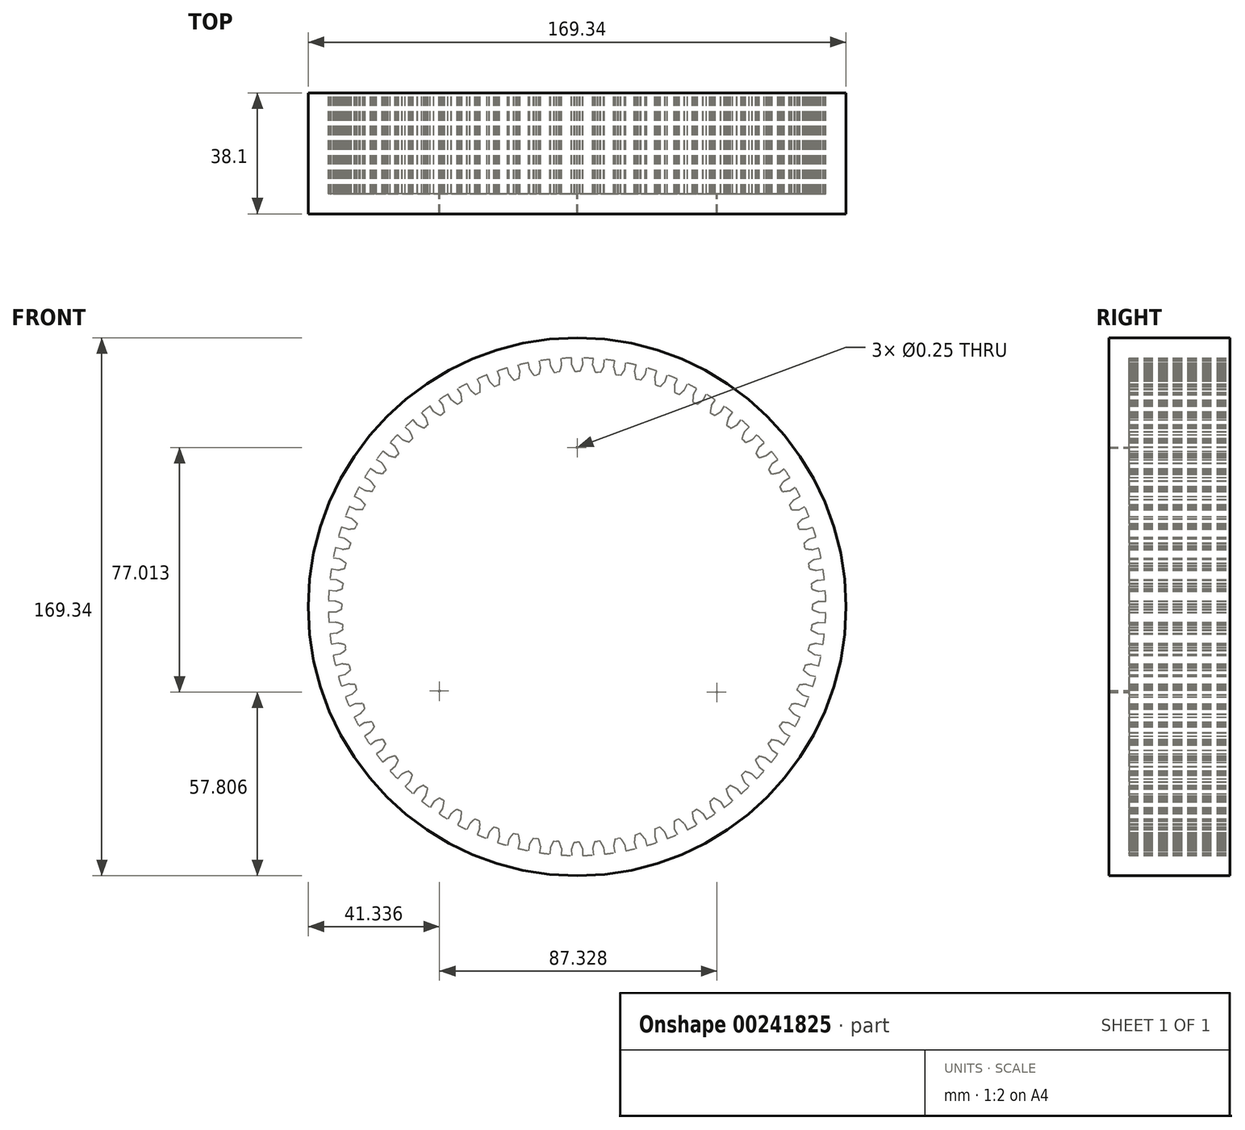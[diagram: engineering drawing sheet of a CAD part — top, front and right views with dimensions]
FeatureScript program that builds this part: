
annotation { "Feature Type Name" : "Feature", "Feature Type Description" : "" }
export const myFeature = defineFeature(function(context is Context, id is Id, definition is map)
    precondition{}
    {
        {
            var Q0;
            Q0=qCreatedBy(makeId("Front.planeOp"),FACE);
            var sketch = newSketch(context, id + "F0", { "sketchPlane" : qUnion([Q0])});
            skCircle(sketch, "E0", {"center": v(0, 0) * mm, "radius": 78.32 * mm});
            skPoint(sketch, "E1", {"position": v(1.7, -156.6) * mm});
            skArc(sketch, "E2.trimOffspring", {"start": v(1.7, -76.18) * mm, "mid": v(1.25, -75.12) * mm, "end": v(0.73, -74.08) * mm});
            skLineSegment(sketch, "E3", {"start": v(1.7, -76.18) * mm, "end": v(1.75, -78.3) * mm});
            skLineSegment(sketch, "E4", {"start": v(0.73, -74.08) * mm, "end": v(-0.1, -74.09) * mm});
            skLineSegment(sketch, "E5.MirrorCS", {"start": v(-0.92, -74.12) * mm, "end": v(-0.1, -74.09) * mm});
            skArc(sketch, "E6.MirrorCS", {"start": v(-1.8, -76.26) * mm, "mid": v(-1.4, -75.17) * mm, "end": v(-0.92, -74.12) * mm});
            skLineSegment(sketch, "E7.MirrorCS", {"start": v(-1.8, -76.26) * mm, "end": v(-1.76, -78.3) * mm});
            skLineSegment(sketch, "E8.1.0", {"start": v(4.85, -76.12) * mm, "end": v(5.08, -78.15) * mm});
            skArc(sketch, "E8.1.1", {"start": v(4.85, -76.12) * mm, "mid": v(5.17, -75) * mm, "end": v(5.55, -73.91) * mm});
            skLineSegment(sketch, "E8.1.2", {"start": v(5.55, -73.91) * mm, "end": v(6.37, -73.81) * mm});
            skLineSegment(sketch, "E8.1.3", {"start": v(7.19, -73.73) * mm, "end": v(6.37, -73.81) * mm});
            skArc(sketch, "E8.1.4", {"start": v(8.34, -75.74) * mm, "mid": v(7.8, -74.72) * mm, "end": v(7.19, -73.73) * mm});
            skLineSegment(sketch, "E8.1.5", {"start": v(8.34, -75.74) * mm, "end": v(8.57, -77.85) * mm});
            skLineSegment(sketch, "E8.2.0", {"start": v(11.47, -75.41) * mm, "end": v(11.87, -77.41) * mm});
            skArc(sketch, "E8.2.1", {"start": v(11.47, -75.41) * mm, "mid": v(11.68, -74.27) * mm, "end": v(11.97, -73.15) * mm});
            skLineSegment(sketch, "E8.2.2", {"start": v(11.97, -73.15) * mm, "end": v(12.77, -72.98) * mm});
            skLineSegment(sketch, "E8.2.3", {"start": v(13.58, -72.83) * mm, "end": v(12.77, -72.98) * mm});
            skArc(sketch, "E8.2.4", {"start": v(14.91, -74.73) * mm, "mid": v(14.28, -73.76) * mm, "end": v(13.58, -72.83) * mm});
            skLineSegment(sketch, "E8.2.5", {"start": v(14.91, -74.73) * mm, "end": v(15.32, -76.8) * mm});
            skLineSegment(sketch, "E8.3.0", {"start": v(18, -74.12) * mm, "end": v(18.57, -76.08) * mm});
            skArc(sketch, "E8.3.1", {"start": v(18, -74.12) * mm, "mid": v(18.11, -72.97) * mm, "end": v(18.3, -71.83) * mm});
            skLineSegment(sketch, "E8.3.2", {"start": v(18.3, -71.83) * mm, "end": v(19.09, -71.59) * mm});
            skLineSegment(sketch, "E8.3.3", {"start": v(19.88, -71.37) * mm, "end": v(19.09, -71.59) * mm});
            skArc(sketch, "E8.3.4", {"start": v(21.37, -73.14) * mm, "mid": v(20.65, -72.23) * mm, "end": v(19.88, -71.37) * mm});
            skLineSegment(sketch, "E8.3.5", {"start": v(21.37, -73.14) * mm, "end": v(21.96, -75.17) * mm});
            skLineSegment(sketch, "E8.4.0", {"start": v(24.4, -72.27) * mm, "end": v(25.13, -74.17) * mm});
            skArc(sketch, "E8.4.1", {"start": v(24.4, -72.27) * mm, "mid": v(24.4, -71.11) * mm, "end": v(24.49, -69.96) * mm});
            skLineSegment(sketch, "E8.4.2", {"start": v(24.49, -69.96) * mm, "end": v(25.25, -69.65) * mm});
            skLineSegment(sketch, "E8.4.3", {"start": v(26.02, -69.36) * mm, "end": v(25.25, -69.65) * mm});
            skArc(sketch, "E8.4.4", {"start": v(27.66, -71) * mm, "mid": v(26.87, -70.16) * mm, "end": v(26.02, -69.36) * mm});
            skLineSegment(sketch, "E8.4.5", {"start": v(27.66, -71) * mm, "end": v(28.43, -72.97) * mm});
            skLineSegment(sketch, "E8.5.0", {"start": v(30.6, -69.87) * mm, "end": v(31.5, -71.7) * mm});
            skArc(sketch, "E8.5.1", {"start": v(30.6, -69.87) * mm, "mid": v(30.5, -68.72) * mm, "end": v(30.5, -67.56) * mm});
            skLineSegment(sketch, "E8.5.2", {"start": v(30.5, -67.56) * mm, "end": v(31.23, -67.19) * mm});
            skLineSegment(sketch, "E8.5.3", {"start": v(31.97, -66.83) * mm, "end": v(31.23, -67.19) * mm});
            skArc(sketch, "E8.5.4", {"start": v(33.74, -68.32) * mm, "mid": v(32.88, -67.55) * mm, "end": v(31.97, -66.83) * mm});
            skLineSegment(sketch, "E8.5.5", {"start": v(33.74, -68.32) * mm, "end": v(34.68, -70.22) * mm});
            skLineSegment(sketch, "E8.6.0", {"start": v(36.57, -66.94) * mm, "end": v(37.63, -68.68) * mm});
            skArc(sketch, "E8.6.1", {"start": v(36.57, -66.94) * mm, "mid": v(36.38, -65.8) * mm, "end": v(36.26, -64.64) * mm});
            skLineSegment(sketch, "E8.6.2", {"start": v(36.26, -64.64) * mm, "end": v(36.96, -64.2) * mm});
            skLineSegment(sketch, "E8.6.3", {"start": v(37.67, -63.79) * mm, "end": v(36.96, -64.2) * mm});
            skArc(sketch, "E8.6.4", {"start": v(39.57, -65.12) * mm, "mid": v(38.64, -64.43) * mm, "end": v(37.67, -63.79) * mm});
            skLineSegment(sketch, "E8.6.5", {"start": v(39.57, -65.12) * mm, "end": v(40.67, -66.93) * mm});
            skLineSegment(sketch, "E8.7.0", {"start": v(42.27, -63.5) * mm, "end": v(43.47, -65.14) * mm});
            skArc(sketch, "E8.7.1", {"start": v(42.27, -63.5) * mm, "mid": v(41.98, -62.38) * mm, "end": v(41.76, -61.24) * mm});
            skLineSegment(sketch, "E8.7.2", {"start": v(41.76, -61.24) * mm, "end": v(42.42, -60.74) * mm});
            skLineSegment(sketch, "E8.7.3", {"start": v(43.09, -60.26) * mm, "end": v(42.42, -60.74) * mm});
            skArc(sketch, "E8.7.4", {"start": v(45.1, -61.42) * mm, "mid": v(44.11, -60.81) * mm, "end": v(43.09, -60.26) * mm});
            skLineSegment(sketch, "E8.7.5", {"start": v(45.1, -61.42) * mm, "end": v(46.35, -63.13) * mm});
            skLineSegment(sketch, "E8.8.0", {"start": v(47.64, -59.57) * mm, "end": v(48.98, -61.1) * mm});
            skArc(sketch, "E8.8.1", {"start": v(47.64, -59.57) * mm, "mid": v(47.25, -58.48) * mm, "end": v(46.94, -57.36) * mm});
            skLineSegment(sketch, "E8.8.2", {"start": v(46.94, -57.36) * mm, "end": v(47.55, -56.81) * mm});
            skLineSegment(sketch, "E8.8.3", {"start": v(48.18, -56.28) * mm, "end": v(47.55, -56.81) * mm});
            skArc(sketch, "E8.8.4", {"start": v(50.28, -57.26) * mm, "mid": v(49.24, -56.74) * mm, "end": v(48.18, -56.28) * mm});
            skLineSegment(sketch, "E8.8.5", {"start": v(50.28, -57.26) * mm, "end": v(51.67, -58.85) * mm});
            skLineSegment(sketch, "E8.9.0", {"start": v(52.65, -55.2) * mm, "end": v(54.12, -56.6) * mm});
            skArc(sketch, "E8.9.1", {"start": v(52.65, -55.2) * mm, "mid": v(52.17, -54.14) * mm, "end": v(51.76, -53.06) * mm});
            skLineSegment(sketch, "E8.9.2", {"start": v(51.76, -53.06) * mm, "end": v(52.32, -52.45) * mm});
            skLineSegment(sketch, "E8.9.3", {"start": v(52.9, -51.86) * mm, "end": v(52.32, -52.45) * mm});
            skArc(sketch, "E8.9.4", {"start": v(55.08, -52.66) * mm, "mid": v(54, -52.23) * mm, "end": v(52.9, -51.86) * mm});
            skLineSegment(sketch, "E8.9.5", {"start": v(55.08, -52.66) * mm, "end": v(56.6, -54.12) * mm});
            skLineSegment(sketch, "E8.10.0", {"start": v(57.26, -50.4) * mm, "end": v(58.85, -51.67) * mm});
            skArc(sketch, "E8.10.1", {"start": v(57.26, -50.4) * mm, "mid": v(56.7, -49.39) * mm, "end": v(56.19, -48.34) * mm});
            skLineSegment(sketch, "E8.10.2", {"start": v(56.19, -48.34) * mm, "end": v(56.7, -47.7) * mm});
            skLineSegment(sketch, "E8.10.3", {"start": v(57.22, -47.06) * mm, "end": v(56.7, -47.7) * mm});
            skArc(sketch, "E8.10.4", {"start": v(59.46, -47.66) * mm, "mid": v(58.35, -47.32) * mm, "end": v(57.22, -47.06) * mm});
            skLineSegment(sketch, "E8.10.5", {"start": v(59.46, -47.66) * mm, "end": v(61.1, -48.98) * mm});
            skLineSegment(sketch, "E8.11.0", {"start": v(61.43, -45.21) * mm, "end": v(63.13, -46.35) * mm});
            skArc(sketch, "E8.11.1", {"start": v(61.43, -45.21) * mm, "mid": v(60.78, -44.26) * mm, "end": v(60.19, -43.26) * mm});
            skLineSegment(sketch, "E8.11.2", {"start": v(60.19, -43.26) * mm, "end": v(60.64, -42.57) * mm});
            skLineSegment(sketch, "E8.11.3", {"start": v(61.1, -41.9) * mm, "end": v(60.64, -42.57) * mm});
            skArc(sketch, "E8.11.4", {"start": v(63.38, -42.3) * mm, "mid": v(62.25, -42.06) * mm, "end": v(61.1, -41.9) * mm});
            skLineSegment(sketch, "E8.11.5", {"start": v(63.38, -42.3) * mm, "end": v(65.14, -43.47) * mm});
            skLineSegment(sketch, "E8.12.0", {"start": v(65.14, -39.69) * mm, "end": v(66.93, -40.67) * mm});
            skArc(sketch, "E8.12.1", {"start": v(65.14, -39.69) * mm, "mid": v(64.4, -38.8) * mm, "end": v(63.73, -37.85) * mm});
            skLineSegment(sketch, "E8.12.2", {"start": v(63.73, -37.85) * mm, "end": v(64.12, -37.12) * mm});
            skLineSegment(sketch, "E8.12.3", {"start": v(64.52, -36.4) * mm, "end": v(64.12, -37.12) * mm});
            skArc(sketch, "E8.12.4", {"start": v(66.83, -36.61) * mm, "mid": v(65.68, -36.47) * mm, "end": v(64.52, -36.4) * mm});
            skLineSegment(sketch, "E8.12.5", {"start": v(66.83, -36.61) * mm, "end": v(68.68, -37.63) * mm});
            skLineSegment(sketch, "E8.13.0", {"start": v(68.35, -33.86) * mm, "end": v(70.22, -34.68) * mm});
            skArc(sketch, "E8.13.1", {"start": v(68.35, -33.86) * mm, "mid": v(67.54, -33.03) * mm, "end": v(66.78, -32.15) * mm});
            skLineSegment(sketch, "E8.13.2", {"start": v(66.78, -32.15) * mm, "end": v(67.1, -31.4) * mm});
            skLineSegment(sketch, "E8.13.3", {"start": v(67.45, -30.64) * mm, "end": v(67.1, -31.4) * mm});
            skArc(sketch, "E8.13.4", {"start": v(69.77, -30.65) * mm, "mid": v(68.6, -30.61) * mm, "end": v(67.45, -30.64) * mm});
            skLineSegment(sketch, "E8.13.5", {"start": v(69.77, -30.65) * mm, "end": v(71.7, -31.5) * mm});
            skLineSegment(sketch, "E8.14.0", {"start": v(71.04, -27.77) * mm, "end": v(72.97, -28.43) * mm});
            skArc(sketch, "E8.14.1", {"start": v(71.04, -27.77) * mm, "mid": v(70.16, -27.02) * mm, "end": v(69.33, -26.2) * mm});
            skLineSegment(sketch, "E8.14.2", {"start": v(69.33, -26.2) * mm, "end": v(69.59, -25.43) * mm});
            skLineSegment(sketch, "E8.14.3", {"start": v(69.86, -24.65) * mm, "end": v(69.59, -25.43) * mm});
            skArc(sketch, "E8.14.4", {"start": v(72.17, -24.45) * mm, "mid": v(71.01, -24.51) * mm, "end": v(69.86, -24.65) * mm});
            skLineSegment(sketch, "E8.14.5", {"start": v(72.17, -24.45) * mm, "end": v(74.17, -25.13) * mm});
            skLineSegment(sketch, "E8.15.0", {"start": v(73.2, -21.48) * mm, "end": v(75.17, -21.96) * mm});
            skArc(sketch, "E8.15.1", {"start": v(73.2, -21.48) * mm, "mid": v(72.25, -20.8) * mm, "end": v(71.35, -20.07) * mm});
            skLineSegment(sketch, "E8.15.2", {"start": v(71.35, -20.07) * mm, "end": v(71.54, -19.26) * mm});
            skLineSegment(sketch, "E8.15.3", {"start": v(71.74, -18.47) * mm, "end": v(71.54, -19.26) * mm});
            skArc(sketch, "E8.15.4", {"start": v(74.03, -18.07) * mm, "mid": v(72.88, -18.23) * mm, "end": v(71.74, -18.47) * mm});
            skLineSegment(sketch, "E8.15.5", {"start": v(74.03, -18.07) * mm, "end": v(76.08, -18.57) * mm});
            skLineSegment(sketch, "E8.16.0", {"start": v(74.79, -15.01) * mm, "end": v(76.8, -15.32) * mm});
            skArc(sketch, "E8.16.1", {"start": v(74.79, -15.01) * mm, "mid": v(73.79, -14.42) * mm, "end": v(72.83, -13.77) * mm});
            skLineSegment(sketch, "E8.16.2", {"start": v(72.83, -13.77) * mm, "end": v(72.95, -12.96) * mm});
            skLineSegment(sketch, "E8.16.3", {"start": v(73.08, -12.14) * mm, "end": v(72.95, -12.96) * mm});
            skArc(sketch, "E8.16.4", {"start": v(75.32, -11.55) * mm, "mid": v(74.2, -11.81) * mm, "end": v(73.08, -12.14) * mm});
            skLineSegment(sketch, "E8.16.5", {"start": v(75.32, -11.55) * mm, "end": v(77.41, -11.87) * mm});
            skLineSegment(sketch, "E8.17.0", {"start": v(75.81, -8.44) * mm, "end": v(77.85, -8.57) * mm});
            skArc(sketch, "E8.17.1", {"start": v(75.81, -8.44) * mm, "mid": v(74.77, -7.94) * mm, "end": v(73.75, -7.37) * mm});
            skLineSegment(sketch, "E8.17.2", {"start": v(73.75, -7.37) * mm, "end": v(73.8, -6.55) * mm});
            skLineSegment(sketch, "E8.17.3", {"start": v(73.86, -5.73) * mm, "end": v(73.8, -6.55) * mm});
            skArc(sketch, "E8.17.4", {"start": v(76.04, -4.94) * mm, "mid": v(74.94, -5.3) * mm, "end": v(73.86, -5.73) * mm});
            skLineSegment(sketch, "E8.17.5", {"start": v(76.04, -4.94) * mm, "end": v(78.15, -5.08) * mm});
            skLineSegment(sketch, "E8.18.0", {"start": v(76.26, -1.8) * mm, "end": v(78.3, -1.76) * mm});
            skArc(sketch, "E8.18.1", {"start": v(76.26, -1.8) * mm, "mid": v(75.17, -1.4) * mm, "end": v(74.12, -0.92) * mm});
            skLineSegment(sketch, "E8.18.2", {"start": v(74.12, -0.92) * mm, "end": v(74.09, -0.1) * mm});
            skLineSegment(sketch, "E8.18.3", {"start": v(74.08, 0.73) * mm, "end": v(74.09, -0.1) * mm});
            skArc(sketch, "E8.18.4", {"start": v(76.18, 1.7) * mm, "mid": v(75.12, 1.25) * mm, "end": v(74.08, 0.73) * mm});
            skLineSegment(sketch, "E8.18.5", {"start": v(76.18, 1.7) * mm, "end": v(78.3, 1.75) * mm});
            skLineSegment(sketch, "E8.19.0", {"start": v(76.12, 4.85) * mm, "end": v(78.15, 5.08) * mm});
            skArc(sketch, "E8.19.1", {"start": v(76.12, 4.85) * mm, "mid": v(75, 5.17) * mm, "end": v(73.91, 5.55) * mm});
            skLineSegment(sketch, "E8.19.2", {"start": v(73.91, 5.55) * mm, "end": v(73.81, 6.37) * mm});
            skLineSegment(sketch, "E8.19.3", {"start": v(73.73, 7.19) * mm, "end": v(73.81, 6.37) * mm});
            skArc(sketch, "E8.19.4", {"start": v(75.74, 8.34) * mm, "mid": v(74.72, 7.8) * mm, "end": v(73.73, 7.19) * mm});
            skLineSegment(sketch, "E8.19.5", {"start": v(75.74, 8.34) * mm, "end": v(77.85, 8.57) * mm});
            skLineSegment(sketch, "E8.20.0", {"start": v(75.41, 11.47) * mm, "end": v(77.41, 11.87) * mm});
            skArc(sketch, "E8.20.1", {"start": v(75.41, 11.47) * mm, "mid": v(74.27, 11.68) * mm, "end": v(73.15, 11.97) * mm});
            skLineSegment(sketch, "E8.20.2", {"start": v(73.15, 11.97) * mm, "end": v(72.98, 12.77) * mm});
            skLineSegment(sketch, "E8.20.3", {"start": v(72.83, 13.58) * mm, "end": v(72.98, 12.77) * mm});
            skArc(sketch, "E8.20.4", {"start": v(74.73, 14.91) * mm, "mid": v(73.76, 14.28) * mm, "end": v(72.83, 13.58) * mm});
            skLineSegment(sketch, "E8.20.5", {"start": v(74.73, 14.91) * mm, "end": v(76.8, 15.32) * mm});
            skLineSegment(sketch, "E8.21.0", {"start": v(74.12, 18) * mm, "end": v(76.08, 18.57) * mm});
            skArc(sketch, "E8.21.1", {"start": v(74.12, 18) * mm, "mid": v(72.97, 18.11) * mm, "end": v(71.83, 18.3) * mm});
            skLineSegment(sketch, "E8.21.2", {"start": v(71.83, 18.3) * mm, "end": v(71.59, 19.09) * mm});
            skLineSegment(sketch, "E8.21.3", {"start": v(71.37, 19.88) * mm, "end": v(71.59, 19.09) * mm});
            skArc(sketch, "E8.21.4", {"start": v(73.14, 21.37) * mm, "mid": v(72.23, 20.65) * mm, "end": v(71.37, 19.88) * mm});
            skLineSegment(sketch, "E8.21.5", {"start": v(73.14, 21.37) * mm, "end": v(75.17, 21.96) * mm});
            skLineSegment(sketch, "E8.22.0", {"start": v(72.27, 24.4) * mm, "end": v(74.17, 25.13) * mm});
            skArc(sketch, "E8.22.1", {"start": v(72.27, 24.4) * mm, "mid": v(71.11, 24.4) * mm, "end": v(69.96, 24.49) * mm});
            skLineSegment(sketch, "E8.22.2", {"start": v(69.96, 24.49) * mm, "end": v(69.65, 25.25) * mm});
            skLineSegment(sketch, "E8.22.3", {"start": v(69.36, 26.02) * mm, "end": v(69.65, 25.25) * mm});
            skArc(sketch, "E8.22.4", {"start": v(71, 27.66) * mm, "mid": v(70.16, 26.87) * mm, "end": v(69.36, 26.02) * mm});
            skLineSegment(sketch, "E8.22.5", {"start": v(71, 27.66) * mm, "end": v(72.97, 28.43) * mm});
            skLineSegment(sketch, "E8.23.0", {"start": v(69.87, 30.6) * mm, "end": v(71.7, 31.5) * mm});
            skArc(sketch, "E8.23.1", {"start": v(69.87, 30.6) * mm, "mid": v(68.72, 30.5) * mm, "end": v(67.56, 30.5) * mm});
            skLineSegment(sketch, "E8.23.2", {"start": v(67.56, 30.5) * mm, "end": v(67.19, 31.23) * mm});
            skLineSegment(sketch, "E8.23.3", {"start": v(66.83, 31.97) * mm, "end": v(67.19, 31.23) * mm});
            skArc(sketch, "E8.23.4", {"start": v(68.32, 33.74) * mm, "mid": v(67.55, 32.88) * mm, "end": v(66.83, 31.97) * mm});
            skLineSegment(sketch, "E8.23.5", {"start": v(68.32, 33.74) * mm, "end": v(70.22, 34.68) * mm});
            skLineSegment(sketch, "E8.24.0", {"start": v(66.94, 36.57) * mm, "end": v(68.68, 37.63) * mm});
            skArc(sketch, "E8.24.1", {"start": v(66.94, 36.57) * mm, "mid": v(65.8, 36.38) * mm, "end": v(64.64, 36.26) * mm});
            skLineSegment(sketch, "E8.24.2", {"start": v(64.64, 36.26) * mm, "end": v(64.2, 36.96) * mm});
            skLineSegment(sketch, "E8.24.3", {"start": v(63.79, 37.67) * mm, "end": v(64.2, 36.96) * mm});
            skArc(sketch, "E8.24.4", {"start": v(65.12, 39.57) * mm, "mid": v(64.43, 38.64) * mm, "end": v(63.79, 37.67) * mm});
            skLineSegment(sketch, "E8.24.5", {"start": v(65.12, 39.57) * mm, "end": v(66.93, 40.67) * mm});
            skLineSegment(sketch, "E8.25.0", {"start": v(63.5, 42.27) * mm, "end": v(65.14, 43.47) * mm});
            skArc(sketch, "E8.25.1", {"start": v(63.5, 42.27) * mm, "mid": v(62.38, 41.98) * mm, "end": v(61.24, 41.76) * mm});
            skLineSegment(sketch, "E8.25.2", {"start": v(61.24, 41.76) * mm, "end": v(60.74, 42.42) * mm});
            skLineSegment(sketch, "E8.25.3", {"start": v(60.26, 43.09) * mm, "end": v(60.74, 42.42) * mm});
            skArc(sketch, "E8.25.4", {"start": v(61.42, 45.1) * mm, "mid": v(60.81, 44.11) * mm, "end": v(60.26, 43.09) * mm});
            skLineSegment(sketch, "E8.25.5", {"start": v(61.42, 45.1) * mm, "end": v(63.13, 46.35) * mm});
            skLineSegment(sketch, "E8.26.0", {"start": v(59.57, 47.64) * mm, "end": v(61.1, 48.98) * mm});
            skArc(sketch, "E8.26.1", {"start": v(59.57, 47.64) * mm, "mid": v(58.48, 47.25) * mm, "end": v(57.36, 46.94) * mm});
            skLineSegment(sketch, "E8.26.2", {"start": v(57.36, 46.94) * mm, "end": v(56.81, 47.55) * mm});
            skLineSegment(sketch, "E8.26.3", {"start": v(56.28, 48.18) * mm, "end": v(56.81, 47.55) * mm});
            skArc(sketch, "E8.26.4", {"start": v(57.26, 50.28) * mm, "mid": v(56.74, 49.24) * mm, "end": v(56.28, 48.18) * mm});
            skLineSegment(sketch, "E8.26.5", {"start": v(57.26, 50.28) * mm, "end": v(58.85, 51.67) * mm});
            skLineSegment(sketch, "E8.27.0", {"start": v(55.2, 52.65) * mm, "end": v(56.6, 54.12) * mm});
            skArc(sketch, "E8.27.1", {"start": v(55.2, 52.65) * mm, "mid": v(54.14, 52.17) * mm, "end": v(53.06, 51.76) * mm});
            skLineSegment(sketch, "E8.27.2", {"start": v(53.06, 51.76) * mm, "end": v(52.45, 52.32) * mm});
            skLineSegment(sketch, "E8.27.3", {"start": v(51.86, 52.9) * mm, "end": v(52.45, 52.32) * mm});
            skArc(sketch, "E8.27.4", {"start": v(52.66, 55.08) * mm, "mid": v(52.23, 54) * mm, "end": v(51.86, 52.9) * mm});
            skLineSegment(sketch, "E8.27.5", {"start": v(52.66, 55.08) * mm, "end": v(54.12, 56.6) * mm});
            skLineSegment(sketch, "E8.28.0", {"start": v(50.4, 57.26) * mm, "end": v(51.67, 58.85) * mm});
            skArc(sketch, "E8.28.1", {"start": v(50.4, 57.26) * mm, "mid": v(49.39, 56.7) * mm, "end": v(48.34, 56.19) * mm});
            skLineSegment(sketch, "E8.28.2", {"start": v(48.34, 56.19) * mm, "end": v(47.7, 56.7) * mm});
            skLineSegment(sketch, "E8.28.3", {"start": v(47.06, 57.22) * mm, "end": v(47.7, 56.7) * mm});
            skArc(sketch, "E8.28.4", {"start": v(47.66, 59.46) * mm, "mid": v(47.32, 58.35) * mm, "end": v(47.06, 57.22) * mm});
            skLineSegment(sketch, "E8.28.5", {"start": v(47.66, 59.46) * mm, "end": v(48.98, 61.1) * mm});
            skLineSegment(sketch, "E8.29.0", {"start": v(45.21, 61.43) * mm, "end": v(46.35, 63.13) * mm});
            skArc(sketch, "E8.29.1", {"start": v(45.21, 61.43) * mm, "mid": v(44.26, 60.78) * mm, "end": v(43.26, 60.19) * mm});
            skLineSegment(sketch, "E8.29.2", {"start": v(43.26, 60.19) * mm, "end": v(42.57, 60.64) * mm});
            skLineSegment(sketch, "E8.29.3", {"start": v(41.9, 61.1) * mm, "end": v(42.57, 60.64) * mm});
            skArc(sketch, "E8.29.4", {"start": v(42.3, 63.38) * mm, "mid": v(42.06, 62.25) * mm, "end": v(41.9, 61.1) * mm});
            skLineSegment(sketch, "E8.29.5", {"start": v(42.3, 63.38) * mm, "end": v(43.47, 65.14) * mm});
            skLineSegment(sketch, "E8.30.0", {"start": v(39.69, 65.14) * mm, "end": v(40.67, 66.93) * mm});
            skArc(sketch, "E8.30.1", {"start": v(39.69, 65.14) * mm, "mid": v(38.8, 64.4) * mm, "end": v(37.85, 63.73) * mm});
            skLineSegment(sketch, "E8.30.2", {"start": v(37.85, 63.73) * mm, "end": v(37.12, 64.12) * mm});
            skLineSegment(sketch, "E8.30.3", {"start": v(36.4, 64.52) * mm, "end": v(37.12, 64.12) * mm});
            skArc(sketch, "E8.30.4", {"start": v(36.61, 66.83) * mm, "mid": v(36.47, 65.68) * mm, "end": v(36.4, 64.52) * mm});
            skLineSegment(sketch, "E8.30.5", {"start": v(36.61, 66.83) * mm, "end": v(37.63, 68.68) * mm});
            skLineSegment(sketch, "E8.31.0", {"start": v(33.86, 68.35) * mm, "end": v(34.68, 70.22) * mm});
            skArc(sketch, "E8.31.1", {"start": v(33.86, 68.35) * mm, "mid": v(33.03, 67.54) * mm, "end": v(32.15, 66.78) * mm});
            skLineSegment(sketch, "E8.31.2", {"start": v(32.15, 66.78) * mm, "end": v(31.4, 67.1) * mm});
            skLineSegment(sketch, "E8.31.3", {"start": v(30.64, 67.45) * mm, "end": v(31.4, 67.1) * mm});
            skArc(sketch, "E8.31.4", {"start": v(30.65, 69.77) * mm, "mid": v(30.61, 68.6) * mm, "end": v(30.64, 67.45) * mm});
            skLineSegment(sketch, "E8.31.5", {"start": v(30.65, 69.77) * mm, "end": v(31.5, 71.7) * mm});
            skLineSegment(sketch, "E8.32.0", {"start": v(27.77, 71.04) * mm, "end": v(28.43, 72.97) * mm});
            skArc(sketch, "E8.32.1", {"start": v(27.77, 71.04) * mm, "mid": v(27.02, 70.16) * mm, "end": v(26.2, 69.33) * mm});
            skLineSegment(sketch, "E8.32.2", {"start": v(26.2, 69.33) * mm, "end": v(25.43, 69.59) * mm});
            skLineSegment(sketch, "E8.32.3", {"start": v(24.65, 69.86) * mm, "end": v(25.43, 69.59) * mm});
            skArc(sketch, "E8.32.4", {"start": v(24.45, 72.17) * mm, "mid": v(24.51, 71.01) * mm, "end": v(24.65, 69.86) * mm});
            skLineSegment(sketch, "E8.32.5", {"start": v(24.45, 72.17) * mm, "end": v(25.13, 74.17) * mm});
            skLineSegment(sketch, "E8.33.0", {"start": v(21.48, 73.2) * mm, "end": v(21.96, 75.17) * mm});
            skArc(sketch, "E8.33.1", {"start": v(21.48, 73.2) * mm, "mid": v(20.8, 72.25) * mm, "end": v(20.07, 71.35) * mm});
            skLineSegment(sketch, "E8.33.2", {"start": v(20.07, 71.35) * mm, "end": v(19.26, 71.54) * mm});
            skLineSegment(sketch, "E8.33.3", {"start": v(18.47, 71.74) * mm, "end": v(19.26, 71.54) * mm});
            skArc(sketch, "E8.33.4", {"start": v(18.07, 74.03) * mm, "mid": v(18.23, 72.88) * mm, "end": v(18.47, 71.74) * mm});
            skLineSegment(sketch, "E8.33.5", {"start": v(18.07, 74.03) * mm, "end": v(18.57, 76.08) * mm});
            skLineSegment(sketch, "E8.34.0", {"start": v(15.01, 74.79) * mm, "end": v(15.32, 76.8) * mm});
            skArc(sketch, "E8.34.1", {"start": v(15.01, 74.79) * mm, "mid": v(14.42, 73.79) * mm, "end": v(13.77, 72.83) * mm});
            skLineSegment(sketch, "E8.34.2", {"start": v(13.77, 72.83) * mm, "end": v(12.96, 72.95) * mm});
            skLineSegment(sketch, "E8.34.3", {"start": v(12.14, 73.08) * mm, "end": v(12.96, 72.95) * mm});
            skArc(sketch, "E8.34.4", {"start": v(11.55, 75.32) * mm, "mid": v(11.81, 74.2) * mm, "end": v(12.14, 73.08) * mm});
            skLineSegment(sketch, "E8.34.5", {"start": v(11.55, 75.32) * mm, "end": v(11.87, 77.41) * mm});
            skLineSegment(sketch, "E8.35.0", {"start": v(8.44, 75.81) * mm, "end": v(8.57, 77.85) * mm});
            skArc(sketch, "E8.35.1", {"start": v(8.44, 75.81) * mm, "mid": v(7.94, 74.77) * mm, "end": v(7.37, 73.75) * mm});
            skLineSegment(sketch, "E8.35.2", {"start": v(7.37, 73.75) * mm, "end": v(6.55, 73.8) * mm});
            skLineSegment(sketch, "E8.35.3", {"start": v(5.73, 73.86) * mm, "end": v(6.55, 73.8) * mm});
            skArc(sketch, "E8.35.4", {"start": v(4.94, 76.04) * mm, "mid": v(5.3, 74.94) * mm, "end": v(5.73, 73.86) * mm});
            skLineSegment(sketch, "E8.35.5", {"start": v(4.94, 76.04) * mm, "end": v(5.08, 78.15) * mm});
            skLineSegment(sketch, "E8.36.0", {"start": v(1.8, 76.26) * mm, "end": v(1.76, 78.3) * mm});
            skArc(sketch, "E8.36.1", {"start": v(1.8, 76.26) * mm, "mid": v(1.4, 75.17) * mm, "end": v(0.92, 74.12) * mm});
            skLineSegment(sketch, "E8.36.2", {"start": v(0.92, 74.12) * mm, "end": v(0.1, 74.09) * mm});
            skLineSegment(sketch, "E8.36.3", {"start": v(-0.73, 74.08) * mm, "end": v(0.1, 74.09) * mm});
            skArc(sketch, "E8.36.4", {"start": v(-1.7, 76.18) * mm, "mid": v(-1.25, 75.12) * mm, "end": v(-0.73, 74.08) * mm});
            skLineSegment(sketch, "E8.36.5", {"start": v(-1.7, 76.18) * mm, "end": v(-1.75, 78.3) * mm});
            skLineSegment(sketch, "E8.37.0", {"start": v(-4.85, 76.12) * mm, "end": v(-5.08, 78.15) * mm});
            skArc(sketch, "E8.37.1", {"start": v(-4.85, 76.12) * mm, "mid": v(-5.17, 75) * mm, "end": v(-5.55, 73.91) * mm});
            skLineSegment(sketch, "E8.37.2", {"start": v(-5.55, 73.91) * mm, "end": v(-6.37, 73.81) * mm});
            skLineSegment(sketch, "E8.37.3", {"start": v(-7.19, 73.73) * mm, "end": v(-6.37, 73.81) * mm});
            skArc(sketch, "E8.37.4", {"start": v(-8.34, 75.74) * mm, "mid": v(-7.8, 74.72) * mm, "end": v(-7.19, 73.73) * mm});
            skLineSegment(sketch, "E8.37.5", {"start": v(-8.34, 75.74) * mm, "end": v(-8.57, 77.85) * mm});
            skLineSegment(sketch, "E8.38.0", {"start": v(-11.47, 75.41) * mm, "end": v(-11.87, 77.41) * mm});
            skArc(sketch, "E8.38.1", {"start": v(-11.47, 75.41) * mm, "mid": v(-11.68, 74.27) * mm, "end": v(-11.97, 73.15) * mm});
            skLineSegment(sketch, "E8.38.2", {"start": v(-11.97, 73.15) * mm, "end": v(-12.77, 72.98) * mm});
            skLineSegment(sketch, "E8.38.3", {"start": v(-13.58, 72.83) * mm, "end": v(-12.77, 72.98) * mm});
            skArc(sketch, "E8.38.4", {"start": v(-14.91, 74.73) * mm, "mid": v(-14.28, 73.76) * mm, "end": v(-13.58, 72.83) * mm});
            skLineSegment(sketch, "E8.38.5", {"start": v(-14.91, 74.73) * mm, "end": v(-15.32, 76.8) * mm});
            skLineSegment(sketch, "E8.39.0", {"start": v(-18, 74.12) * mm, "end": v(-18.57, 76.08) * mm});
            skArc(sketch, "E8.39.1", {"start": v(-18, 74.12) * mm, "mid": v(-18.11, 72.97) * mm, "end": v(-18.3, 71.83) * mm});
            skLineSegment(sketch, "E8.39.2", {"start": v(-18.3, 71.83) * mm, "end": v(-19.09, 71.59) * mm});
            skLineSegment(sketch, "E8.39.3", {"start": v(-19.88, 71.37) * mm, "end": v(-19.09, 71.59) * mm});
            skArc(sketch, "E8.39.4", {"start": v(-21.37, 73.14) * mm, "mid": v(-20.65, 72.23) * mm, "end": v(-19.88, 71.37) * mm});
            skLineSegment(sketch, "E8.39.5", {"start": v(-21.37, 73.14) * mm, "end": v(-21.96, 75.17) * mm});
            skLineSegment(sketch, "E8.40.0", {"start": v(-24.4, 72.27) * mm, "end": v(-25.13, 74.17) * mm});
            skArc(sketch, "E8.40.1", {"start": v(-24.4, 72.27) * mm, "mid": v(-24.4, 71.11) * mm, "end": v(-24.49, 69.96) * mm});
            skLineSegment(sketch, "E8.40.2", {"start": v(-24.49, 69.96) * mm, "end": v(-25.25, 69.65) * mm});
            skLineSegment(sketch, "E8.40.3", {"start": v(-26.02, 69.36) * mm, "end": v(-25.25, 69.65) * mm});
            skArc(sketch, "E8.40.4", {"start": v(-27.66, 71) * mm, "mid": v(-26.87, 70.16) * mm, "end": v(-26.02, 69.36) * mm});
            skLineSegment(sketch, "E8.40.5", {"start": v(-27.66, 71) * mm, "end": v(-28.43, 72.97) * mm});
            skLineSegment(sketch, "E8.41.0", {"start": v(-30.6, 69.87) * mm, "end": v(-31.5, 71.7) * mm});
            skArc(sketch, "E8.41.1", {"start": v(-30.6, 69.87) * mm, "mid": v(-30.5, 68.72) * mm, "end": v(-30.5, 67.56) * mm});
            skLineSegment(sketch, "E8.41.2", {"start": v(-30.5, 67.56) * mm, "end": v(-31.23, 67.19) * mm});
            skLineSegment(sketch, "E8.41.3", {"start": v(-31.97, 66.83) * mm, "end": v(-31.23, 67.19) * mm});
            skArc(sketch, "E8.41.4", {"start": v(-33.74, 68.32) * mm, "mid": v(-32.88, 67.55) * mm, "end": v(-31.97, 66.83) * mm});
            skLineSegment(sketch, "E8.41.5", {"start": v(-33.74, 68.32) * mm, "end": v(-34.68, 70.22) * mm});
            skLineSegment(sketch, "E8.42.0", {"start": v(-36.57, 66.94) * mm, "end": v(-37.63, 68.68) * mm});
            skArc(sketch, "E8.42.1", {"start": v(-36.57, 66.94) * mm, "mid": v(-36.38, 65.8) * mm, "end": v(-36.26, 64.64) * mm});
            skLineSegment(sketch, "E8.42.2", {"start": v(-36.26, 64.64) * mm, "end": v(-36.96, 64.2) * mm});
            skLineSegment(sketch, "E8.42.3", {"start": v(-37.67, 63.79) * mm, "end": v(-36.96, 64.2) * mm});
            skArc(sketch, "E8.42.4", {"start": v(-39.57, 65.12) * mm, "mid": v(-38.64, 64.43) * mm, "end": v(-37.67, 63.79) * mm});
            skLineSegment(sketch, "E8.42.5", {"start": v(-39.57, 65.12) * mm, "end": v(-40.67, 66.93) * mm});
            skLineSegment(sketch, "E8.43.0", {"start": v(-42.27, 63.5) * mm, "end": v(-43.47, 65.14) * mm});
            skArc(sketch, "E8.43.1", {"start": v(-42.27, 63.5) * mm, "mid": v(-41.98, 62.38) * mm, "end": v(-41.76, 61.24) * mm});
            skLineSegment(sketch, "E8.43.2", {"start": v(-41.76, 61.24) * mm, "end": v(-42.42, 60.74) * mm});
            skLineSegment(sketch, "E8.43.3", {"start": v(-43.09, 60.26) * mm, "end": v(-42.42, 60.74) * mm});
            skArc(sketch, "E8.43.4", {"start": v(-45.1, 61.42) * mm, "mid": v(-44.11, 60.81) * mm, "end": v(-43.09, 60.26) * mm});
            skLineSegment(sketch, "E8.43.5", {"start": v(-45.1, 61.42) * mm, "end": v(-46.35, 63.13) * mm});
            skLineSegment(sketch, "E8.44.0", {"start": v(-47.64, 59.57) * mm, "end": v(-48.98, 61.1) * mm});
            skArc(sketch, "E8.44.1", {"start": v(-47.64, 59.57) * mm, "mid": v(-47.25, 58.48) * mm, "end": v(-46.94, 57.36) * mm});
            skLineSegment(sketch, "E8.44.2", {"start": v(-46.94, 57.36) * mm, "end": v(-47.55, 56.81) * mm});
            skLineSegment(sketch, "E8.44.3", {"start": v(-48.18, 56.28) * mm, "end": v(-47.55, 56.81) * mm});
            skArc(sketch, "E8.44.4", {"start": v(-50.28, 57.26) * mm, "mid": v(-49.24, 56.74) * mm, "end": v(-48.18, 56.28) * mm});
            skLineSegment(sketch, "E8.44.5", {"start": v(-50.28, 57.26) * mm, "end": v(-51.67, 58.85) * mm});
            skLineSegment(sketch, "E8.45.0", {"start": v(-52.65, 55.2) * mm, "end": v(-54.12, 56.6) * mm});
            skArc(sketch, "E8.45.1", {"start": v(-52.65, 55.2) * mm, "mid": v(-52.17, 54.14) * mm, "end": v(-51.76, 53.06) * mm});
            skLineSegment(sketch, "E8.45.2", {"start": v(-51.76, 53.06) * mm, "end": v(-52.32, 52.45) * mm});
            skLineSegment(sketch, "E8.45.3", {"start": v(-52.9, 51.86) * mm, "end": v(-52.32, 52.45) * mm});
            skArc(sketch, "E8.45.4", {"start": v(-55.08, 52.66) * mm, "mid": v(-54, 52.23) * mm, "end": v(-52.9, 51.86) * mm});
            skLineSegment(sketch, "E8.45.5", {"start": v(-55.08, 52.66) * mm, "end": v(-56.6, 54.12) * mm});
            skLineSegment(sketch, "E8.46.0", {"start": v(-57.26, 50.4) * mm, "end": v(-58.85, 51.67) * mm});
            skArc(sketch, "E8.46.1", {"start": v(-57.26, 50.4) * mm, "mid": v(-56.7, 49.39) * mm, "end": v(-56.19, 48.34) * mm});
            skLineSegment(sketch, "E8.46.2", {"start": v(-56.19, 48.34) * mm, "end": v(-56.7, 47.7) * mm});
            skLineSegment(sketch, "E8.46.3", {"start": v(-57.22, 47.06) * mm, "end": v(-56.7, 47.7) * mm});
            skArc(sketch, "E8.46.4", {"start": v(-59.46, 47.66) * mm, "mid": v(-58.35, 47.32) * mm, "end": v(-57.22, 47.06) * mm});
            skLineSegment(sketch, "E8.46.5", {"start": v(-59.46, 47.66) * mm, "end": v(-61.1, 48.98) * mm});
            skLineSegment(sketch, "E8.47.0", {"start": v(-61.43, 45.21) * mm, "end": v(-63.13, 46.35) * mm});
            skArc(sketch, "E8.47.1", {"start": v(-61.43, 45.21) * mm, "mid": v(-60.78, 44.26) * mm, "end": v(-60.19, 43.26) * mm});
            skLineSegment(sketch, "E8.47.2", {"start": v(-60.19, 43.26) * mm, "end": v(-60.64, 42.57) * mm});
            skLineSegment(sketch, "E8.47.3", {"start": v(-61.1, 41.9) * mm, "end": v(-60.64, 42.57) * mm});
            skArc(sketch, "E8.47.4", {"start": v(-63.38, 42.3) * mm, "mid": v(-62.25, 42.06) * mm, "end": v(-61.1, 41.9) * mm});
            skLineSegment(sketch, "E8.47.5", {"start": v(-63.38, 42.3) * mm, "end": v(-65.14, 43.47) * mm});
            skLineSegment(sketch, "E8.48.0", {"start": v(-65.14, 39.69) * mm, "end": v(-66.93, 40.67) * mm});
            skArc(sketch, "E8.48.1", {"start": v(-65.14, 39.69) * mm, "mid": v(-64.4, 38.8) * mm, "end": v(-63.73, 37.85) * mm});
            skLineSegment(sketch, "E8.48.2", {"start": v(-63.73, 37.85) * mm, "end": v(-64.12, 37.12) * mm});
            skLineSegment(sketch, "E8.48.3", {"start": v(-64.52, 36.4) * mm, "end": v(-64.12, 37.12) * mm});
            skArc(sketch, "E8.48.4", {"start": v(-66.83, 36.61) * mm, "mid": v(-65.68, 36.47) * mm, "end": v(-64.52, 36.4) * mm});
            skLineSegment(sketch, "E8.48.5", {"start": v(-66.83, 36.61) * mm, "end": v(-68.68, 37.63) * mm});
            skLineSegment(sketch, "E8.49.0", {"start": v(-68.35, 33.86) * mm, "end": v(-70.22, 34.68) * mm});
            skArc(sketch, "E8.49.1", {"start": v(-68.35, 33.86) * mm, "mid": v(-67.54, 33.03) * mm, "end": v(-66.78, 32.15) * mm});
            skLineSegment(sketch, "E8.49.2", {"start": v(-66.78, 32.15) * mm, "end": v(-67.1, 31.4) * mm});
            skLineSegment(sketch, "E8.49.3", {"start": v(-67.45, 30.64) * mm, "end": v(-67.1, 31.4) * mm});
            skArc(sketch, "E8.49.4", {"start": v(-69.77, 30.65) * mm, "mid": v(-68.6, 30.61) * mm, "end": v(-67.45, 30.64) * mm});
            skLineSegment(sketch, "E8.49.5", {"start": v(-69.77, 30.65) * mm, "end": v(-71.7, 31.5) * mm});
            skLineSegment(sketch, "E8.50.0", {"start": v(-71.04, 27.77) * mm, "end": v(-72.97, 28.43) * mm});
            skArc(sketch, "E8.50.1", {"start": v(-71.04, 27.77) * mm, "mid": v(-70.16, 27.02) * mm, "end": v(-69.33, 26.2) * mm});
            skLineSegment(sketch, "E8.50.2", {"start": v(-69.33, 26.2) * mm, "end": v(-69.59, 25.43) * mm});
            skLineSegment(sketch, "E8.50.3", {"start": v(-69.86, 24.65) * mm, "end": v(-69.59, 25.43) * mm});
            skArc(sketch, "E8.50.4", {"start": v(-72.17, 24.45) * mm, "mid": v(-71.01, 24.51) * mm, "end": v(-69.86, 24.65) * mm});
            skLineSegment(sketch, "E8.50.5", {"start": v(-72.17, 24.45) * mm, "end": v(-74.17, 25.13) * mm});
            skLineSegment(sketch, "E8.51.0", {"start": v(-73.2, 21.48) * mm, "end": v(-75.17, 21.96) * mm});
            skArc(sketch, "E8.51.1", {"start": v(-73.2, 21.48) * mm, "mid": v(-72.25, 20.8) * mm, "end": v(-71.35, 20.07) * mm});
            skLineSegment(sketch, "E8.51.2", {"start": v(-71.35, 20.07) * mm, "end": v(-71.54, 19.26) * mm});
            skLineSegment(sketch, "E8.51.3", {"start": v(-71.74, 18.47) * mm, "end": v(-71.54, 19.26) * mm});
            skArc(sketch, "E8.51.4", {"start": v(-74.03, 18.07) * mm, "mid": v(-72.88, 18.23) * mm, "end": v(-71.74, 18.47) * mm});
            skLineSegment(sketch, "E8.51.5", {"start": v(-74.03, 18.07) * mm, "end": v(-76.08, 18.57) * mm});
            skLineSegment(sketch, "E8.52.0", {"start": v(-74.79, 15.01) * mm, "end": v(-76.8, 15.32) * mm});
            skArc(sketch, "E8.52.1", {"start": v(-74.79, 15.01) * mm, "mid": v(-73.79, 14.42) * mm, "end": v(-72.83, 13.77) * mm});
            skLineSegment(sketch, "E8.52.2", {"start": v(-72.83, 13.77) * mm, "end": v(-72.95, 12.96) * mm});
            skLineSegment(sketch, "E8.52.3", {"start": v(-73.08, 12.14) * mm, "end": v(-72.95, 12.96) * mm});
            skArc(sketch, "E8.52.4", {"start": v(-75.32, 11.55) * mm, "mid": v(-74.2, 11.81) * mm, "end": v(-73.08, 12.14) * mm});
            skLineSegment(sketch, "E8.52.5", {"start": v(-75.32, 11.55) * mm, "end": v(-77.41, 11.87) * mm});
            skLineSegment(sketch, "E8.53.0", {"start": v(-75.81, 8.44) * mm, "end": v(-77.85, 8.57) * mm});
            skArc(sketch, "E8.53.1", {"start": v(-75.81, 8.44) * mm, "mid": v(-74.77, 7.94) * mm, "end": v(-73.75, 7.37) * mm});
            skLineSegment(sketch, "E8.53.2", {"start": v(-73.75, 7.37) * mm, "end": v(-73.8, 6.55) * mm});
            skLineSegment(sketch, "E8.53.3", {"start": v(-73.86, 5.73) * mm, "end": v(-73.8, 6.55) * mm});
            skArc(sketch, "E8.53.4", {"start": v(-76.04, 4.94) * mm, "mid": v(-74.94, 5.3) * mm, "end": v(-73.86, 5.73) * mm});
            skLineSegment(sketch, "E8.53.5", {"start": v(-76.04, 4.94) * mm, "end": v(-78.15, 5.08) * mm});
            skLineSegment(sketch, "E8.54.0", {"start": v(-76.26, 1.8) * mm, "end": v(-78.3, 1.76) * mm});
            skArc(sketch, "E8.54.1", {"start": v(-76.26, 1.8) * mm, "mid": v(-75.17, 1.4) * mm, "end": v(-74.12, 0.92) * mm});
            skLineSegment(sketch, "E8.54.2", {"start": v(-74.12, 0.92) * mm, "end": v(-74.09, 0.1) * mm});
            skLineSegment(sketch, "E8.54.3", {"start": v(-74.08, -0.73) * mm, "end": v(-74.09, 0.1) * mm});
            skArc(sketch, "E8.54.4", {"start": v(-76.18, -1.7) * mm, "mid": v(-75.12, -1.25) * mm, "end": v(-74.08, -0.73) * mm});
            skLineSegment(sketch, "E8.54.5", {"start": v(-76.18, -1.7) * mm, "end": v(-78.3, -1.75) * mm});
            skLineSegment(sketch, "E8.55.0", {"start": v(-76.12, -4.85) * mm, "end": v(-78.15, -5.08) * mm});
            skArc(sketch, "E8.55.1", {"start": v(-76.12, -4.85) * mm, "mid": v(-75, -5.17) * mm, "end": v(-73.91, -5.55) * mm});
            skLineSegment(sketch, "E8.55.2", {"start": v(-73.91, -5.55) * mm, "end": v(-73.81, -6.37) * mm});
            skLineSegment(sketch, "E8.55.3", {"start": v(-73.73, -7.19) * mm, "end": v(-73.81, -6.37) * mm});
            skArc(sketch, "E8.55.4", {"start": v(-75.74, -8.34) * mm, "mid": v(-74.72, -7.8) * mm, "end": v(-73.73, -7.19) * mm});
            skLineSegment(sketch, "E8.55.5", {"start": v(-75.74, -8.34) * mm, "end": v(-77.85, -8.57) * mm});
            skLineSegment(sketch, "E8.56.0", {"start": v(-75.41, -11.47) * mm, "end": v(-77.41, -11.87) * mm});
            skArc(sketch, "E8.56.1", {"start": v(-75.41, -11.47) * mm, "mid": v(-74.27, -11.68) * mm, "end": v(-73.15, -11.97) * mm});
            skLineSegment(sketch, "E8.56.2", {"start": v(-73.15, -11.97) * mm, "end": v(-72.98, -12.77) * mm});
            skLineSegment(sketch, "E8.56.3", {"start": v(-72.83, -13.58) * mm, "end": v(-72.98, -12.77) * mm});
            skArc(sketch, "E8.56.4", {"start": v(-74.73, -14.91) * mm, "mid": v(-73.76, -14.28) * mm, "end": v(-72.83, -13.58) * mm});
            skLineSegment(sketch, "E8.56.5", {"start": v(-74.73, -14.91) * mm, "end": v(-76.8, -15.32) * mm});
            skLineSegment(sketch, "E8.57.0", {"start": v(-74.12, -18) * mm, "end": v(-76.08, -18.57) * mm});
            skArc(sketch, "E8.57.1", {"start": v(-74.12, -18) * mm, "mid": v(-72.97, -18.11) * mm, "end": v(-71.83, -18.3) * mm});
            skLineSegment(sketch, "E8.57.2", {"start": v(-71.83, -18.3) * mm, "end": v(-71.59, -19.09) * mm});
            skLineSegment(sketch, "E8.57.3", {"start": v(-71.37, -19.88) * mm, "end": v(-71.59, -19.09) * mm});
            skArc(sketch, "E8.57.4", {"start": v(-73.14, -21.37) * mm, "mid": v(-72.23, -20.65) * mm, "end": v(-71.37, -19.88) * mm});
            skLineSegment(sketch, "E8.57.5", {"start": v(-73.14, -21.37) * mm, "end": v(-75.17, -21.96) * mm});
            skLineSegment(sketch, "E8.58.0", {"start": v(-72.27, -24.4) * mm, "end": v(-74.17, -25.13) * mm});
            skArc(sketch, "E8.58.1", {"start": v(-72.27, -24.4) * mm, "mid": v(-71.11, -24.4) * mm, "end": v(-69.96, -24.49) * mm});
            skLineSegment(sketch, "E8.58.2", {"start": v(-69.96, -24.49) * mm, "end": v(-69.65, -25.25) * mm});
            skLineSegment(sketch, "E8.58.3", {"start": v(-69.36, -26.02) * mm, "end": v(-69.65, -25.25) * mm});
            skArc(sketch, "E8.58.4", {"start": v(-71, -27.66) * mm, "mid": v(-70.16, -26.87) * mm, "end": v(-69.36, -26.02) * mm});
            skLineSegment(sketch, "E8.58.5", {"start": v(-71, -27.66) * mm, "end": v(-72.97, -28.43) * mm});
            skLineSegment(sketch, "E8.59.0", {"start": v(-69.87, -30.6) * mm, "end": v(-71.7, -31.5) * mm});
            skArc(sketch, "E8.59.1", {"start": v(-69.87, -30.6) * mm, "mid": v(-68.72, -30.5) * mm, "end": v(-67.56, -30.5) * mm});
            skLineSegment(sketch, "E8.59.2", {"start": v(-67.56, -30.5) * mm, "end": v(-67.19, -31.23) * mm});
            skLineSegment(sketch, "E8.59.3", {"start": v(-66.83, -31.97) * mm, "end": v(-67.19, -31.23) * mm});
            skArc(sketch, "E8.59.4", {"start": v(-68.32, -33.74) * mm, "mid": v(-67.55, -32.88) * mm, "end": v(-66.83, -31.97) * mm});
            skLineSegment(sketch, "E8.59.5", {"start": v(-68.32, -33.74) * mm, "end": v(-70.22, -34.68) * mm});
            skLineSegment(sketch, "E8.60.0", {"start": v(-66.94, -36.57) * mm, "end": v(-68.68, -37.63) * mm});
            skArc(sketch, "E8.60.1", {"start": v(-66.94, -36.57) * mm, "mid": v(-65.8, -36.38) * mm, "end": v(-64.64, -36.26) * mm});
            skLineSegment(sketch, "E8.60.2", {"start": v(-64.64, -36.26) * mm, "end": v(-64.2, -36.96) * mm});
            skLineSegment(sketch, "E8.60.3", {"start": v(-63.79, -37.67) * mm, "end": v(-64.2, -36.96) * mm});
            skArc(sketch, "E8.60.4", {"start": v(-65.12, -39.57) * mm, "mid": v(-64.43, -38.64) * mm, "end": v(-63.79, -37.67) * mm});
            skLineSegment(sketch, "E8.60.5", {"start": v(-65.12, -39.57) * mm, "end": v(-66.93, -40.67) * mm});
            skLineSegment(sketch, "E8.61.0", {"start": v(-63.5, -42.27) * mm, "end": v(-65.14, -43.47) * mm});
            skArc(sketch, "E8.61.1", {"start": v(-63.5, -42.27) * mm, "mid": v(-62.38, -41.98) * mm, "end": v(-61.24, -41.76) * mm});
            skLineSegment(sketch, "E8.61.2", {"start": v(-61.24, -41.76) * mm, "end": v(-60.74, -42.42) * mm});
            skLineSegment(sketch, "E8.61.3", {"start": v(-60.26, -43.09) * mm, "end": v(-60.74, -42.42) * mm});
            skArc(sketch, "E8.61.4", {"start": v(-61.42, -45.1) * mm, "mid": v(-60.81, -44.11) * mm, "end": v(-60.26, -43.09) * mm});
            skLineSegment(sketch, "E8.61.5", {"start": v(-61.42, -45.1) * mm, "end": v(-63.13, -46.35) * mm});
            skLineSegment(sketch, "E8.62.0", {"start": v(-59.57, -47.64) * mm, "end": v(-61.1, -48.98) * mm});
            skArc(sketch, "E8.62.1", {"start": v(-59.57, -47.64) * mm, "mid": v(-58.48, -47.25) * mm, "end": v(-57.36, -46.94) * mm});
            skLineSegment(sketch, "E8.62.2", {"start": v(-57.36, -46.94) * mm, "end": v(-56.81, -47.55) * mm});
            skLineSegment(sketch, "E8.62.3", {"start": v(-56.28, -48.18) * mm, "end": v(-56.81, -47.55) * mm});
            skArc(sketch, "E8.62.4", {"start": v(-57.26, -50.28) * mm, "mid": v(-56.74, -49.24) * mm, "end": v(-56.28, -48.18) * mm});
            skLineSegment(sketch, "E8.62.5", {"start": v(-57.26, -50.28) * mm, "end": v(-58.85, -51.67) * mm});
            skLineSegment(sketch, "E8.63.0", {"start": v(-55.2, -52.65) * mm, "end": v(-56.6, -54.12) * mm});
            skArc(sketch, "E8.63.1", {"start": v(-55.2, -52.65) * mm, "mid": v(-54.14, -52.17) * mm, "end": v(-53.06, -51.76) * mm});
            skLineSegment(sketch, "E8.63.2", {"start": v(-53.06, -51.76) * mm, "end": v(-52.45, -52.32) * mm});
            skLineSegment(sketch, "E8.63.3", {"start": v(-51.86, -52.9) * mm, "end": v(-52.45, -52.32) * mm});
            skArc(sketch, "E8.63.4", {"start": v(-52.66, -55.08) * mm, "mid": v(-52.23, -54) * mm, "end": v(-51.86, -52.9) * mm});
            skLineSegment(sketch, "E8.63.5", {"start": v(-52.66, -55.08) * mm, "end": v(-54.12, -56.6) * mm});
            skLineSegment(sketch, "E8.64.0", {"start": v(-50.4, -57.26) * mm, "end": v(-51.67, -58.85) * mm});
            skArc(sketch, "E8.64.1", {"start": v(-50.4, -57.26) * mm, "mid": v(-49.39, -56.7) * mm, "end": v(-48.34, -56.19) * mm});
            skLineSegment(sketch, "E8.64.2", {"start": v(-48.34, -56.19) * mm, "end": v(-47.7, -56.7) * mm});
            skLineSegment(sketch, "E8.64.3", {"start": v(-47.06, -57.22) * mm, "end": v(-47.7, -56.7) * mm});
            skArc(sketch, "E8.64.4", {"start": v(-47.66, -59.46) * mm, "mid": v(-47.32, -58.35) * mm, "end": v(-47.06, -57.22) * mm});
            skLineSegment(sketch, "E8.64.5", {"start": v(-47.66, -59.46) * mm, "end": v(-48.98, -61.1) * mm});
            skLineSegment(sketch, "E8.65.0", {"start": v(-45.21, -61.43) * mm, "end": v(-46.35, -63.13) * mm});
            skArc(sketch, "E8.65.1", {"start": v(-45.21, -61.43) * mm, "mid": v(-44.26, -60.78) * mm, "end": v(-43.26, -60.19) * mm});
            skLineSegment(sketch, "E8.65.2", {"start": v(-43.26, -60.19) * mm, "end": v(-42.57, -60.64) * mm});
            skLineSegment(sketch, "E8.65.3", {"start": v(-41.9, -61.1) * mm, "end": v(-42.57, -60.64) * mm});
            skArc(sketch, "E8.65.4", {"start": v(-42.3, -63.38) * mm, "mid": v(-42.06, -62.25) * mm, "end": v(-41.9, -61.1) * mm});
            skLineSegment(sketch, "E8.65.5", {"start": v(-42.3, -63.38) * mm, "end": v(-43.47, -65.14) * mm});
            skLineSegment(sketch, "E8.66.0", {"start": v(-39.69, -65.14) * mm, "end": v(-40.67, -66.93) * mm});
            skArc(sketch, "E8.66.1", {"start": v(-39.69, -65.14) * mm, "mid": v(-38.8, -64.4) * mm, "end": v(-37.85, -63.73) * mm});
            skLineSegment(sketch, "E8.66.2", {"start": v(-37.85, -63.73) * mm, "end": v(-37.12, -64.12) * mm});
            skLineSegment(sketch, "E8.66.3", {"start": v(-36.4, -64.52) * mm, "end": v(-37.12, -64.12) * mm});
            skArc(sketch, "E8.66.4", {"start": v(-36.61, -66.83) * mm, "mid": v(-36.47, -65.68) * mm, "end": v(-36.4, -64.52) * mm});
            skLineSegment(sketch, "E8.66.5", {"start": v(-36.61, -66.83) * mm, "end": v(-37.63, -68.68) * mm});
            skLineSegment(sketch, "E8.67.0", {"start": v(-33.86, -68.35) * mm, "end": v(-34.68, -70.22) * mm});
            skArc(sketch, "E8.67.1", {"start": v(-33.86, -68.35) * mm, "mid": v(-33.03, -67.54) * mm, "end": v(-32.15, -66.78) * mm});
            skLineSegment(sketch, "E8.67.2", {"start": v(-32.15, -66.78) * mm, "end": v(-31.4, -67.1) * mm});
            skLineSegment(sketch, "E8.67.3", {"start": v(-30.64, -67.45) * mm, "end": v(-31.4, -67.1) * mm});
            skArc(sketch, "E8.67.4", {"start": v(-30.65, -69.77) * mm, "mid": v(-30.61, -68.6) * mm, "end": v(-30.64, -67.45) * mm});
            skLineSegment(sketch, "E8.67.5", {"start": v(-30.65, -69.77) * mm, "end": v(-31.5, -71.7) * mm});
            skLineSegment(sketch, "E8.68.0", {"start": v(-27.77, -71.04) * mm, "end": v(-28.43, -72.97) * mm});
            skArc(sketch, "E8.68.1", {"start": v(-27.77, -71.04) * mm, "mid": v(-27.02, -70.16) * mm, "end": v(-26.2, -69.33) * mm});
            skLineSegment(sketch, "E8.68.2", {"start": v(-26.2, -69.33) * mm, "end": v(-25.43, -69.59) * mm});
            skLineSegment(sketch, "E8.68.3", {"start": v(-24.65, -69.86) * mm, "end": v(-25.43, -69.59) * mm});
            skArc(sketch, "E8.68.4", {"start": v(-24.45, -72.17) * mm, "mid": v(-24.51, -71.01) * mm, "end": v(-24.65, -69.86) * mm});
            skLineSegment(sketch, "E8.68.5", {"start": v(-24.45, -72.17) * mm, "end": v(-25.13, -74.17) * mm});
            skLineSegment(sketch, "E8.69.0", {"start": v(-21.48, -73.2) * mm, "end": v(-21.96, -75.17) * mm});
            skArc(sketch, "E8.69.1", {"start": v(-21.48, -73.2) * mm, "mid": v(-20.8, -72.25) * mm, "end": v(-20.07, -71.35) * mm});
            skLineSegment(sketch, "E8.69.2", {"start": v(-20.07, -71.35) * mm, "end": v(-19.26, -71.54) * mm});
            skLineSegment(sketch, "E8.69.3", {"start": v(-18.47, -71.74) * mm, "end": v(-19.26, -71.54) * mm});
            skArc(sketch, "E8.69.4", {"start": v(-18.07, -74.03) * mm, "mid": v(-18.23, -72.88) * mm, "end": v(-18.47, -71.74) * mm});
            skLineSegment(sketch, "E8.69.5", {"start": v(-18.07, -74.03) * mm, "end": v(-18.57, -76.08) * mm});
            skLineSegment(sketch, "E8.70.0", {"start": v(-15.01, -74.79) * mm, "end": v(-15.32, -76.8) * mm});
            skArc(sketch, "E8.70.1", {"start": v(-15.01, -74.79) * mm, "mid": v(-14.42, -73.79) * mm, "end": v(-13.77, -72.83) * mm});
            skLineSegment(sketch, "E8.70.2", {"start": v(-13.77, -72.83) * mm, "end": v(-12.96, -72.95) * mm});
            skLineSegment(sketch, "E8.70.3", {"start": v(-12.14, -73.08) * mm, "end": v(-12.96, -72.95) * mm});
            skArc(sketch, "E8.70.4", {"start": v(-11.55, -75.32) * mm, "mid": v(-11.81, -74.2) * mm, "end": v(-12.14, -73.08) * mm});
            skLineSegment(sketch, "E8.70.5", {"start": v(-11.55, -75.32) * mm, "end": v(-11.87, -77.41) * mm});
            skLineSegment(sketch, "E8.71.0", {"start": v(-8.44, -75.81) * mm, "end": v(-8.57, -77.85) * mm});
            skArc(sketch, "E8.71.1", {"start": v(-8.44, -75.81) * mm, "mid": v(-7.94, -74.77) * mm, "end": v(-7.37, -73.75) * mm});
            skLineSegment(sketch, "E8.71.2", {"start": v(-7.37, -73.75) * mm, "end": v(-6.55, -73.8) * mm});
            skLineSegment(sketch, "E8.71.3", {"start": v(-5.73, -73.86) * mm, "end": v(-6.55, -73.8) * mm});
            skArc(sketch, "E8.71.4", {"start": v(-4.94, -76.04) * mm, "mid": v(-5.3, -74.94) * mm, "end": v(-5.73, -73.86) * mm});
            skLineSegment(sketch, "E8.71.5", {"start": v(-4.94, -76.04) * mm, "end": v(-5.08, -78.15) * mm});
            skCircle(sketch, "E9", {"center": v(0, 0) * mm, "radius": 84.67 * mm});
            skSolve(sketch);
        }
        {
            var Q0;
            Q0=makeQuery(id+"F0.imprint","IMPRINT",FACE,{"disambiguationData":[TD([[makeQuery(id+"F0.imprint","IMPRINT",EDGE,{"derivedFrom":sQuery(id+"F0.wireOp",EDGE,"E9")}),1.0]])]});
            var Q1;
            {var subQ0=sQuery(id+"F0.wireOp",EDGE,"E8.53.0");Q1=makeQuery(id+"F0.imprint","IMPRINT",FACE,{"disambiguationData":[TD([[makeQuery(id+"F0.imprint","IMPRINT",EDGE,{"derivedFrom":subQ0}),1.0]])]});}
            var Q2;
            {var subQ0=sQuery(id+"F0.wireOp",EDGE,"E8.52.0");Q2=makeQuery(id+"F0.imprint","IMPRINT",FACE,{"disambiguationData":[TD([[makeQuery(id+"F0.imprint","IMPRINT",EDGE,{"derivedFrom":subQ0}),1.0]])]});}
            var Q3;
            {var subQ0=sQuery(id+"F0.wireOp",EDGE,"E8.51.0");Q3=makeQuery(id+"F0.imprint","IMPRINT",FACE,{"disambiguationData":[TD([[makeQuery(id+"F0.imprint","IMPRINT",EDGE,{"derivedFrom":subQ0}),1.0]])]});}
            var Q4;
            {var subQ0=sQuery(id+"F0.wireOp",EDGE,"E8.50.0");Q4=makeQuery(id+"F0.imprint","IMPRINT",FACE,{"disambiguationData":[TD([[makeQuery(id+"F0.imprint","IMPRINT",EDGE,{"derivedFrom":subQ0}),1.0]])]});}
            var Q5;
            {var subQ0=sQuery(id+"F0.wireOp",EDGE,"E8.49.0");Q5=makeQuery(id+"F0.imprint","IMPRINT",FACE,{"disambiguationData":[TD([[makeQuery(id+"F0.imprint","IMPRINT",EDGE,{"derivedFrom":subQ0}),1.0]])]});}
            var Q6;
            {var subQ0=sQuery(id+"F0.wireOp",EDGE,"E8.48.0");Q6=makeQuery(id+"F0.imprint","IMPRINT",FACE,{"disambiguationData":[TD([[makeQuery(id+"F0.imprint","IMPRINT",EDGE,{"derivedFrom":subQ0}),1.0]])]});}
            var Q7;
            {var subQ0=sQuery(id+"F0.wireOp",EDGE,"E8.47.0");Q7=makeQuery(id+"F0.imprint","IMPRINT",FACE,{"disambiguationData":[TD([[makeQuery(id+"F0.imprint","IMPRINT",EDGE,{"derivedFrom":subQ0}),1.0]])]});}
            var Q8;
            {var subQ1=sQuery(id+"F0.wireOp",EDGE,"E8.46.0");Q8=makeQuery(id+"F0.imprint","IMPRINT",FACE,{"disambiguationData":[TD([[makeQuery(id+"F0.imprint","IMPRINT",EDGE,{"derivedFrom":subQ1}),1.0]])]});}
            var Q9;
            {var subQ0=sQuery(id+"F0.wireOp",EDGE,"E8.45.0");Q9=makeQuery(id+"F0.imprint","IMPRINT",FACE,{"disambiguationData":[TD([[makeQuery(id+"F0.imprint","IMPRINT",EDGE,{"derivedFrom":subQ0}),1.0]])]});}
            var Q10;
            {var subQ0=sQuery(id+"F0.wireOp",EDGE,"E8.44.0");Q10=makeQuery(id+"F0.imprint","IMPRINT",FACE,{"disambiguationData":[TD([[makeQuery(id+"F0.imprint","IMPRINT",EDGE,{"derivedFrom":subQ0}),1.0]])]});}
            var Q11;
            {var subQ0=sQuery(id+"F0.wireOp",EDGE,"E8.43.0");Q11=makeQuery(id+"F0.imprint","IMPRINT",FACE,{"disambiguationData":[TD([[makeQuery(id+"F0.imprint","IMPRINT",EDGE,{"derivedFrom":subQ0}),1.0]])]});}
            var Q12;
            {var subQ0=sQuery(id+"F0.wireOp",EDGE,"E8.42.0");Q12=makeQuery(id+"F0.imprint","IMPRINT",FACE,{"disambiguationData":[TD([[makeQuery(id+"F0.imprint","IMPRINT",EDGE,{"derivedFrom":subQ0}),1.0]])]});}
            var Q13;
            {var subQ1=sQuery(id+"F0.wireOp",EDGE,"E8.41.0");Q13=makeQuery(id+"F0.imprint","IMPRINT",FACE,{"disambiguationData":[TD([[makeQuery(id+"F0.imprint","IMPRINT",EDGE,{"derivedFrom":subQ1}),1.0]])]});}
            var Q14;
            {var subQ0=sQuery(id+"F0.wireOp",EDGE,"E8.40.0");Q14=makeQuery(id+"F0.imprint","IMPRINT",FACE,{"disambiguationData":[TD([[makeQuery(id+"F0.imprint","IMPRINT",EDGE,{"derivedFrom":subQ0}),1.0]])]});}
            var Q15;
            {var subQ0=sQuery(id+"F0.wireOp",EDGE,"E8.39.0");Q15=makeQuery(id+"F0.imprint","IMPRINT",FACE,{"disambiguationData":[TD([[makeQuery(id+"F0.imprint","IMPRINT",EDGE,{"derivedFrom":subQ0}),1.0]])]});}
            var Q16;
            {var subQ0=sQuery(id+"F0.wireOp",EDGE,"E8.38.0");Q16=makeQuery(id+"F0.imprint","IMPRINT",FACE,{"disambiguationData":[TD([[makeQuery(id+"F0.imprint","IMPRINT",EDGE,{"derivedFrom":subQ0}),1.0]])]});}
            var Q17;
            {var subQ0=sQuery(id+"F0.wireOp",EDGE,"E8.37.0");Q17=makeQuery(id+"F0.imprint","IMPRINT",FACE,{"disambiguationData":[TD([[makeQuery(id+"F0.imprint","IMPRINT",EDGE,{"derivedFrom":subQ0}),1.0]])]});}
            var Q18;
            {var subQ0=sQuery(id+"F0.wireOp",EDGE,"E8.36.0");Q18=makeQuery(id+"F0.imprint","IMPRINT",FACE,{"disambiguationData":[TD([[makeQuery(id+"F0.imprint","IMPRINT",EDGE,{"derivedFrom":subQ0}),1.0]])]});}
            var Q19;
            {var subQ0=sQuery(id+"F0.wireOp",EDGE,"E8.35.0");Q19=makeQuery(id+"F0.imprint","IMPRINT",FACE,{"disambiguationData":[TD([[makeQuery(id+"F0.imprint","IMPRINT",EDGE,{"derivedFrom":subQ0}),1.0]])]});}
            var Q20;
            {var subQ0=sQuery(id+"F0.wireOp",EDGE,"E8.34.0");Q20=makeQuery(id+"F0.imprint","IMPRINT",FACE,{"disambiguationData":[TD([[makeQuery(id+"F0.imprint","IMPRINT",EDGE,{"derivedFrom":subQ0}),1.0]])]});}
            var Q21;
            {var subQ1=sQuery(id+"F0.wireOp",EDGE,"E8.33.0");Q21=makeQuery(id+"F0.imprint","IMPRINT",FACE,{"disambiguationData":[TD([[makeQuery(id+"F0.imprint","IMPRINT",EDGE,{"derivedFrom":subQ1}),1.0]])]});}
            var Q22;
            {var subQ0=sQuery(id+"F0.wireOp",EDGE,"E8.32.0");Q22=makeQuery(id+"F0.imprint","IMPRINT",FACE,{"disambiguationData":[TD([[makeQuery(id+"F0.imprint","IMPRINT",EDGE,{"derivedFrom":subQ0}),1.0]])]});}
            var Q23;
            {var subQ0=sQuery(id+"F0.wireOp",EDGE,"E8.31.0");Q23=makeQuery(id+"F0.imprint","IMPRINT",FACE,{"disambiguationData":[TD([[makeQuery(id+"F0.imprint","IMPRINT",EDGE,{"derivedFrom":subQ0}),1.0]])]});}
            var Q24;
            {var subQ0=sQuery(id+"F0.wireOp",EDGE,"E8.30.0");Q24=makeQuery(id+"F0.imprint","IMPRINT",FACE,{"disambiguationData":[TD([[makeQuery(id+"F0.imprint","IMPRINT",EDGE,{"derivedFrom":subQ0}),1.0]])]});}
            var Q25;
            {var subQ0=sQuery(id+"F0.wireOp",EDGE,"E8.29.0");Q25=makeQuery(id+"F0.imprint","IMPRINT",FACE,{"disambiguationData":[TD([[makeQuery(id+"F0.imprint","IMPRINT",EDGE,{"derivedFrom":subQ0}),1.0]])]});}
            var Q26;
            {var subQ0=sQuery(id+"F0.wireOp",EDGE,"E8.28.0");Q26=makeQuery(id+"F0.imprint","IMPRINT",FACE,{"disambiguationData":[TD([[makeQuery(id+"F0.imprint","IMPRINT",EDGE,{"derivedFrom":subQ0}),1.0]])]});}
            var Q27;
            {var subQ0=sQuery(id+"F0.wireOp",EDGE,"E8.27.0");Q27=makeQuery(id+"F0.imprint","IMPRINT",FACE,{"disambiguationData":[TD([[makeQuery(id+"F0.imprint","IMPRINT",EDGE,{"derivedFrom":subQ0}),1.0]])]});}
            var Q28;
            {var subQ0=sQuery(id+"F0.wireOp",EDGE,"E8.26.0");Q28=makeQuery(id+"F0.imprint","IMPRINT",FACE,{"disambiguationData":[TD([[makeQuery(id+"F0.imprint","IMPRINT",EDGE,{"derivedFrom":subQ0}),1.0]])]});}
            var Q29;
            {var subQ0=sQuery(id+"F0.wireOp",EDGE,"E8.25.0");Q29=makeQuery(id+"F0.imprint","IMPRINT",FACE,{"disambiguationData":[TD([[makeQuery(id+"F0.imprint","IMPRINT",EDGE,{"derivedFrom":subQ0}),1.0]])]});}
            var Q30;
            {var subQ0=sQuery(id+"F0.wireOp",EDGE,"E8.24.0");Q30=makeQuery(id+"F0.imprint","IMPRINT",FACE,{"disambiguationData":[TD([[makeQuery(id+"F0.imprint","IMPRINT",EDGE,{"derivedFrom":subQ0}),1.0]])]});}
            var Q31;
            {var subQ0=sQuery(id+"F0.wireOp",EDGE,"E8.23.0");Q31=makeQuery(id+"F0.imprint","IMPRINT",FACE,{"disambiguationData":[TD([[makeQuery(id+"F0.imprint","IMPRINT",EDGE,{"derivedFrom":subQ0}),1.0]])]});}
            var Q32;
            {var subQ0=sQuery(id+"F0.wireOp",EDGE,"E8.22.0");Q32=makeQuery(id+"F0.imprint","IMPRINT",FACE,{"disambiguationData":[TD([[makeQuery(id+"F0.imprint","IMPRINT",EDGE,{"derivedFrom":subQ0}),1.0]])]});}
            var Q33;
            {var subQ0=sQuery(id+"F0.wireOp",EDGE,"E8.21.0");Q33=makeQuery(id+"F0.imprint","IMPRINT",FACE,{"disambiguationData":[TD([[makeQuery(id+"F0.imprint","IMPRINT",EDGE,{"derivedFrom":subQ0}),1.0]])]});}
            var Q34;
            {var subQ0=sQuery(id+"F0.wireOp",EDGE,"E8.20.0");Q34=makeQuery(id+"F0.imprint","IMPRINT",FACE,{"disambiguationData":[TD([[makeQuery(id+"F0.imprint","IMPRINT",EDGE,{"derivedFrom":subQ0}),1.0]])]});}
            var Q35;
            {var subQ0=sQuery(id+"F0.wireOp",EDGE,"E8.19.0");Q35=makeQuery(id+"F0.imprint","IMPRINT",FACE,{"disambiguationData":[TD([[makeQuery(id+"F0.imprint","IMPRINT",EDGE,{"derivedFrom":subQ0}),1.0]])]});}
            var Q36;
            {var subQ0=sQuery(id+"F0.wireOp",EDGE,"E8.18.0");Q36=makeQuery(id+"F0.imprint","IMPRINT",FACE,{"disambiguationData":[TD([[makeQuery(id+"F0.imprint","IMPRINT",EDGE,{"derivedFrom":subQ0}),1.0]])]});}
            var Q37;
            {var subQ0=sQuery(id+"F0.wireOp",EDGE,"E8.17.0");Q37=makeQuery(id+"F0.imprint","IMPRINT",FACE,{"disambiguationData":[TD([[makeQuery(id+"F0.imprint","IMPRINT",EDGE,{"derivedFrom":subQ0}),1.0]])]});}
            var Q38;
            {var subQ0=sQuery(id+"F0.wireOp",EDGE,"E8.16.0");Q38=makeQuery(id+"F0.imprint","IMPRINT",FACE,{"disambiguationData":[TD([[makeQuery(id+"F0.imprint","IMPRINT",EDGE,{"derivedFrom":subQ0}),1.0]])]});}
            var Q39;
            {var subQ0=sQuery(id+"F0.wireOp",EDGE,"E8.15.0");Q39=makeQuery(id+"F0.imprint","IMPRINT",FACE,{"disambiguationData":[TD([[makeQuery(id+"F0.imprint","IMPRINT",EDGE,{"derivedFrom":subQ0}),1.0]])]});}
            var Q40;
            {var subQ0=sQuery(id+"F0.wireOp",EDGE,"E8.14.0");Q40=makeQuery(id+"F0.imprint","IMPRINT",FACE,{"disambiguationData":[TD([[makeQuery(id+"F0.imprint","IMPRINT",EDGE,{"derivedFrom":subQ0}),1.0]])]});}
            var Q41;
            {var subQ1=sQuery(id+"F0.wireOp",EDGE,"E8.13.0");Q41=makeQuery(id+"F0.imprint","IMPRINT",FACE,{"disambiguationData":[TD([[makeQuery(id+"F0.imprint","IMPRINT",EDGE,{"derivedFrom":subQ1}),1.0]])]});}
            var Q42;
            {var subQ0=sQuery(id+"F0.wireOp",EDGE,"E8.12.0");Q42=makeQuery(id+"F0.imprint","IMPRINT",FACE,{"disambiguationData":[TD([[makeQuery(id+"F0.imprint","IMPRINT",EDGE,{"derivedFrom":subQ0}),1.0]])]});}
            var Q43;
            {var subQ0=sQuery(id+"F0.wireOp",EDGE,"E8.11.0");Q43=makeQuery(id+"F0.imprint","IMPRINT",FACE,{"disambiguationData":[TD([[makeQuery(id+"F0.imprint","IMPRINT",EDGE,{"derivedFrom":subQ0}),1.0]])]});}
            var Q44;
            {var subQ0=sQuery(id+"F0.wireOp",EDGE,"E8.10.0");Q44=makeQuery(id+"F0.imprint","IMPRINT",FACE,{"disambiguationData":[TD([[makeQuery(id+"F0.imprint","IMPRINT",EDGE,{"derivedFrom":subQ0}),1.0]])]});}
            var Q45;
            {var subQ0=sQuery(id+"F0.wireOp",EDGE,"E8.9.0");Q45=makeQuery(id+"F0.imprint","IMPRINT",FACE,{"disambiguationData":[TD([[makeQuery(id+"F0.imprint","IMPRINT",EDGE,{"derivedFrom":subQ0}),1.0]])]});}
            var Q46;
            {var subQ0=sQuery(id+"F0.wireOp",EDGE,"E8.8.0");Q46=makeQuery(id+"F0.imprint","IMPRINT",FACE,{"disambiguationData":[TD([[makeQuery(id+"F0.imprint","IMPRINT",EDGE,{"derivedFrom":subQ0}),1.0]])]});}
            var Q47;
            {var subQ0=sQuery(id+"F0.wireOp",EDGE,"E8.7.0");Q47=makeQuery(id+"F0.imprint","IMPRINT",FACE,{"disambiguationData":[TD([[makeQuery(id+"F0.imprint","IMPRINT",EDGE,{"derivedFrom":subQ0}),1.0]])]});}
            var Q48;
            {var subQ0=sQuery(id+"F0.wireOp",EDGE,"E8.6.0");Q48=makeQuery(id+"F0.imprint","IMPRINT",FACE,{"disambiguationData":[TD([[makeQuery(id+"F0.imprint","IMPRINT",EDGE,{"derivedFrom":subQ0}),1.0]])]});}
            var Q49;
            {var subQ0=sQuery(id+"F0.wireOp",EDGE,"E8.5.0");Q49=makeQuery(id+"F0.imprint","IMPRINT",FACE,{"disambiguationData":[TD([[makeQuery(id+"F0.imprint","IMPRINT",EDGE,{"derivedFrom":subQ0}),1.0]])]});}
            var Q50;
            {var subQ0=sQuery(id+"F0.wireOp",EDGE,"E8.4.0");Q50=makeQuery(id+"F0.imprint","IMPRINT",FACE,{"disambiguationData":[TD([[makeQuery(id+"F0.imprint","IMPRINT",EDGE,{"derivedFrom":subQ0}),1.0]])]});}
            var Q51;
            {var subQ0=sQuery(id+"F0.wireOp",EDGE,"E8.3.0");Q51=makeQuery(id+"F0.imprint","IMPRINT",FACE,{"disambiguationData":[TD([[makeQuery(id+"F0.imprint","IMPRINT",EDGE,{"derivedFrom":subQ0}),1.0]])]});}
            var Q52;
            {var subQ0=sQuery(id+"F0.wireOp",EDGE,"E8.2.0");Q52=makeQuery(id+"F0.imprint","IMPRINT",FACE,{"disambiguationData":[TD([[makeQuery(id+"F0.imprint","IMPRINT",EDGE,{"derivedFrom":subQ0}),1.0]])]});}
            var Q53;
            {var subQ0=sQuery(id+"F0.wireOp",EDGE,"E8.1.0");Q53=makeQuery(id+"F0.imprint","IMPRINT",FACE,{"disambiguationData":[TD([[makeQuery(id+"F0.imprint","IMPRINT",EDGE,{"derivedFrom":subQ0}),1.0]])]});}
            var Q54;
            Q54=makeQuery(id+"F0.imprint","IMPRINT",FACE,{"disambiguationData":[TD([[makeQuery(id+"F0.imprint","IMPRINT",EDGE,{"derivedFrom":sQuery(id+"F0.wireOp",EDGE,"E2.trimOffspring")}),1.0]])]});
            var Q55;
            {var subQ0=sQuery(id+"F0.wireOp",EDGE,"E8.71.0");Q55=makeQuery(id+"F0.imprint","IMPRINT",FACE,{"disambiguationData":[TD([[makeQuery(id+"F0.imprint","IMPRINT",EDGE,{"derivedFrom":subQ0}),1.0]])]});}
            var Q56;
            {var subQ0=sQuery(id+"F0.wireOp",EDGE,"E8.70.0");Q56=makeQuery(id+"F0.imprint","IMPRINT",FACE,{"disambiguationData":[TD([[makeQuery(id+"F0.imprint","IMPRINT",EDGE,{"derivedFrom":subQ0}),1.0]])]});}
            var Q57;
            {var subQ0=sQuery(id+"F0.wireOp",EDGE,"E8.69.0");Q57=makeQuery(id+"F0.imprint","IMPRINT",FACE,{"disambiguationData":[TD([[makeQuery(id+"F0.imprint","IMPRINT",EDGE,{"derivedFrom":subQ0}),1.0]])]});}
            var Q58;
            {var subQ0=sQuery(id+"F0.wireOp",EDGE,"E8.68.0");Q58=makeQuery(id+"F0.imprint","IMPRINT",FACE,{"disambiguationData":[TD([[makeQuery(id+"F0.imprint","IMPRINT",EDGE,{"derivedFrom":subQ0}),1.0]])]});}
            var Q59;
            {var subQ0=sQuery(id+"F0.wireOp",EDGE,"E8.67.0");Q59=makeQuery(id+"F0.imprint","IMPRINT",FACE,{"disambiguationData":[TD([[makeQuery(id+"F0.imprint","IMPRINT",EDGE,{"derivedFrom":subQ0}),1.0]])]});}
            var Q60;
            {var subQ1=sQuery(id+"F0.wireOp",EDGE,"E8.66.0");Q60=makeQuery(id+"F0.imprint","IMPRINT",FACE,{"disambiguationData":[TD([[makeQuery(id+"F0.imprint","IMPRINT",EDGE,{"derivedFrom":subQ1}),1.0]])]});}
            var Q61;
            {var subQ0=sQuery(id+"F0.wireOp",EDGE,"E8.65.0");Q61=makeQuery(id+"F0.imprint","IMPRINT",FACE,{"disambiguationData":[TD([[makeQuery(id+"F0.imprint","IMPRINT",EDGE,{"derivedFrom":subQ0}),1.0]])]});}
            var Q62;
            {var subQ0=sQuery(id+"F0.wireOp",EDGE,"E8.64.0");Q62=makeQuery(id+"F0.imprint","IMPRINT",FACE,{"disambiguationData":[TD([[makeQuery(id+"F0.imprint","IMPRINT",EDGE,{"derivedFrom":subQ0}),1.0]])]});}
            var Q63;
            {var subQ0=sQuery(id+"F0.wireOp",EDGE,"E8.63.0");Q63=makeQuery(id+"F0.imprint","IMPRINT",FACE,{"disambiguationData":[TD([[makeQuery(id+"F0.imprint","IMPRINT",EDGE,{"derivedFrom":subQ0}),1.0]])]});}
            var Q64;
            {var subQ0=sQuery(id+"F0.wireOp",EDGE,"E8.62.0");Q64=makeQuery(id+"F0.imprint","IMPRINT",FACE,{"disambiguationData":[TD([[makeQuery(id+"F0.imprint","IMPRINT",EDGE,{"derivedFrom":subQ0}),1.0]])]});}
            var Q65;
            {var subQ0=sQuery(id+"F0.wireOp",EDGE,"E8.60.0");Q65=makeQuery(id+"F0.imprint","IMPRINT",FACE,{"disambiguationData":[TD([[makeQuery(id+"F0.imprint","IMPRINT",EDGE,{"derivedFrom":subQ0}),1.0]])]});}
            var Q66;
            {var subQ0=sQuery(id+"F0.wireOp",EDGE,"E8.61.0");Q66=makeQuery(id+"F0.imprint","IMPRINT",FACE,{"disambiguationData":[TD([[makeQuery(id+"F0.imprint","IMPRINT",EDGE,{"derivedFrom":subQ0}),1.0]])]});}
            var Q67;
            {var subQ0=sQuery(id+"F0.wireOp",EDGE,"E8.59.0");Q67=makeQuery(id+"F0.imprint","IMPRINT",FACE,{"disambiguationData":[TD([[makeQuery(id+"F0.imprint","IMPRINT",EDGE,{"derivedFrom":subQ0}),1.0]])]});}
            var Q68;
            {var subQ0=sQuery(id+"F0.wireOp",EDGE,"E8.58.0");Q68=makeQuery(id+"F0.imprint","IMPRINT",FACE,{"disambiguationData":[TD([[makeQuery(id+"F0.imprint","IMPRINT",EDGE,{"derivedFrom":subQ0}),1.0]])]});}
            var Q69;
            {var subQ0=sQuery(id+"F0.wireOp",EDGE,"E8.57.0");Q69=makeQuery(id+"F0.imprint","IMPRINT",FACE,{"disambiguationData":[TD([[makeQuery(id+"F0.imprint","IMPRINT",EDGE,{"derivedFrom":subQ0}),1.0]])]});}
            var Q70;
            {var subQ0=sQuery(id+"F0.wireOp",EDGE,"E8.56.0");Q70=makeQuery(id+"F0.imprint","IMPRINT",FACE,{"disambiguationData":[TD([[makeQuery(id+"F0.imprint","IMPRINT",EDGE,{"derivedFrom":subQ0}),1.0]])]});}
            var Q71;
            {var subQ0=sQuery(id+"F0.wireOp",EDGE,"E8.55.0");Q71=makeQuery(id+"F0.imprint","IMPRINT",FACE,{"disambiguationData":[TD([[makeQuery(id+"F0.imprint","IMPRINT",EDGE,{"derivedFrom":subQ0}),1.0]])]});}
            var Q72;
            {var subQ0=sQuery(id+"F0.wireOp",EDGE,"E8.54.0");Q72=makeQuery(id+"F0.imprint","IMPRINT",FACE,{"disambiguationData":[TD([[makeQuery(id+"F0.imprint","IMPRINT",EDGE,{"derivedFrom":subQ0}),1.0]])]});}
            extrude(context, id + "F1", {"entities" : qUnion([Q0, Q1, Q2, Q3, Q4, Q5, Q6, Q7, Q8, Q9, Q10, Q11, Q12, Q13, Q14, Q15, Q16, Q17, Q18, Q19, Q20, Q21, Q22, Q23, Q24, Q25, Q26, Q27, Q28, Q29, Q30, Q31, Q32, Q33, Q34, Q35, Q36, Q37, Q38, Q39, Q40, Q41, Q42, Q43, Q44, Q45, Q46, Q47, Q48, Q49, Q50, Q51, Q52, Q53, Q54, Q55, Q56, Q57, Q58, Q59, Q60, Q61, Q62, Q63, Q64, Q65, Q66, Q67, Q68, Q69, Q70, Q71, Q72]), "depth" : 31.75 * mm});
        }
        {
            var Q0;
            Q0=makeQuery(id+"F1.opExtrude","CAP_FACE",FACE,{"disambiguationData":[OSD([sQuery(id+"F0.wireOp",EDGE,"E0"),sQuery(id+"F0.wireOp",EDGE,"E2.trimOffspring"),sQuery(id+"F0.wireOp",EDGE,"E3"),sQuery(id+"F0.wireOp",EDGE,"E4"),sQuery(id+"F0.wireOp",EDGE,"E5.MirrorCS"),sQuery(id+"F0.wireOp",EDGE,"E6.MirrorCS"),sQuery(id+"F0.wireOp",EDGE,"E7.MirrorCS"),sQuery(id+"F0.wireOp",EDGE,"E8.1.0"),sQuery(id+"F0.wireOp",EDGE,"E8.1.1"),sQuery(id+"F0.wireOp",EDGE,"E8.1.2"),sQuery(id+"F0.wireOp",EDGE,"E8.1.3"),sQuery(id+"F0.wireOp",EDGE,"E8.1.4"),sQuery(id+"F0.wireOp",EDGE,"E8.1.5"),sQuery(id+"F0.wireOp",EDGE,"E8.2.0"),sQuery(id+"F0.wireOp",EDGE,"E8.2.1"),sQuery(id+"F0.wireOp",EDGE,"E8.2.2"),sQuery(id+"F0.wireOp",EDGE,"E8.2.3"),sQuery(id+"F0.wireOp",EDGE,"E8.2.4"),sQuery(id+"F0.wireOp",EDGE,"E8.2.5"),sQuery(id+"F0.wireOp",EDGE,"E8.3.0"),sQuery(id+"F0.wireOp",EDGE,"E8.3.1"),sQuery(id+"F0.wireOp",EDGE,"E8.3.2"),sQuery(id+"F0.wireOp",EDGE,"E8.3.3"),sQuery(id+"F0.wireOp",EDGE,"E8.3.4"),sQuery(id+"F0.wireOp",EDGE,"E8.3.5"),sQuery(id+"F0.wireOp",EDGE,"E8.4.0"),sQuery(id+"F0.wireOp",EDGE,"E8.4.1"),sQuery(id+"F0.wireOp",EDGE,"E8.4.2"),sQuery(id+"F0.wireOp",EDGE,"E8.4.3"),sQuery(id+"F0.wireOp",EDGE,"E8.4.4"),sQuery(id+"F0.wireOp",EDGE,"E8.4.5"),sQuery(id+"F0.wireOp",EDGE,"E8.5.0"),sQuery(id+"F0.wireOp",EDGE,"E8.5.1"),sQuery(id+"F0.wireOp",EDGE,"E8.5.2"),sQuery(id+"F0.wireOp",EDGE,"E8.5.3"),sQuery(id+"F0.wireOp",EDGE,"E8.5.4"),sQuery(id+"F0.wireOp",EDGE,"E8.5.5"),sQuery(id+"F0.wireOp",EDGE,"E8.6.0"),sQuery(id+"F0.wireOp",EDGE,"E8.6.1"),sQuery(id+"F0.wireOp",EDGE,"E8.6.2"),sQuery(id+"F0.wireOp",EDGE,"E8.6.3"),sQuery(id+"F0.wireOp",EDGE,"E8.6.4"),sQuery(id+"F0.wireOp",EDGE,"E8.6.5"),sQuery(id+"F0.wireOp",EDGE,"E8.7.0"),sQuery(id+"F0.wireOp",EDGE,"E8.7.1"),sQuery(id+"F0.wireOp",EDGE,"E8.7.2"),sQuery(id+"F0.wireOp",EDGE,"E8.7.3"),sQuery(id+"F0.wireOp",EDGE,"E8.7.4"),sQuery(id+"F0.wireOp",EDGE,"E8.7.5"),sQuery(id+"F0.wireOp",EDGE,"E8.8.0"),sQuery(id+"F0.wireOp",EDGE,"E8.8.1"),sQuery(id+"F0.wireOp",EDGE,"E8.8.2"),sQuery(id+"F0.wireOp",EDGE,"E8.8.3"),sQuery(id+"F0.wireOp",EDGE,"E8.8.4"),sQuery(id+"F0.wireOp",EDGE,"E8.8.5"),sQuery(id+"F0.wireOp",EDGE,"E8.9.0"),sQuery(id+"F0.wireOp",EDGE,"E8.9.1"),sQuery(id+"F0.wireOp",EDGE,"E8.9.2"),sQuery(id+"F0.wireOp",EDGE,"E8.9.3"),sQuery(id+"F0.wireOp",EDGE,"E8.9.4"),sQuery(id+"F0.wireOp",EDGE,"E8.9.5"),sQuery(id+"F0.wireOp",EDGE,"E8.10.0"),sQuery(id+"F0.wireOp",EDGE,"E8.10.1"),sQuery(id+"F0.wireOp",EDGE,"E8.10.2"),sQuery(id+"F0.wireOp",EDGE,"E8.10.3"),sQuery(id+"F0.wireOp",EDGE,"E8.10.4"),sQuery(id+"F0.wireOp",EDGE,"E8.10.5"),sQuery(id+"F0.wireOp",EDGE,"E8.11.0"),sQuery(id+"F0.wireOp",EDGE,"E8.11.1"),sQuery(id+"F0.wireOp",EDGE,"E8.11.2"),sQuery(id+"F0.wireOp",EDGE,"E8.11.3"),sQuery(id+"F0.wireOp",EDGE,"E8.11.4"),sQuery(id+"F0.wireOp",EDGE,"E8.11.5"),sQuery(id+"F0.wireOp",EDGE,"E8.12.0"),sQuery(id+"F0.wireOp",EDGE,"E8.12.1"),sQuery(id+"F0.wireOp",EDGE,"E8.12.2"),sQuery(id+"F0.wireOp",EDGE,"E8.12.3"),sQuery(id+"F0.wireOp",EDGE,"E8.12.4"),sQuery(id+"F0.wireOp",EDGE,"E8.12.5"),sQuery(id+"F0.wireOp",EDGE,"E8.13.0"),sQuery(id+"F0.wireOp",EDGE,"E8.13.1"),sQuery(id+"F0.wireOp",EDGE,"E8.13.2"),sQuery(id+"F0.wireOp",EDGE,"E8.13.3"),sQuery(id+"F0.wireOp",EDGE,"E8.13.4"),sQuery(id+"F0.wireOp",EDGE,"E8.13.5"),sQuery(id+"F0.wireOp",EDGE,"E8.14.0"),sQuery(id+"F0.wireOp",EDGE,"E8.14.1"),sQuery(id+"F0.wireOp",EDGE,"E8.14.2"),sQuery(id+"F0.wireOp",EDGE,"E8.14.3"),sQuery(id+"F0.wireOp",EDGE,"E8.14.4"),sQuery(id+"F0.wireOp",EDGE,"E8.14.5"),sQuery(id+"F0.wireOp",EDGE,"E8.15.0"),sQuery(id+"F0.wireOp",EDGE,"E8.15.1"),sQuery(id+"F0.wireOp",EDGE,"E8.15.2"),sQuery(id+"F0.wireOp",EDGE,"E8.15.3"),sQuery(id+"F0.wireOp",EDGE,"E8.15.4"),sQuery(id+"F0.wireOp",EDGE,"E8.15.5"),sQuery(id+"F0.wireOp",EDGE,"E8.16.0"),sQuery(id+"F0.wireOp",EDGE,"E8.16.1"),sQuery(id+"F0.wireOp",EDGE,"E8.16.2"),sQuery(id+"F0.wireOp",EDGE,"E8.16.3"),sQuery(id+"F0.wireOp",EDGE,"E8.16.4"),sQuery(id+"F0.wireOp",EDGE,"E8.16.5"),sQuery(id+"F0.wireOp",EDGE,"E8.17.0"),sQuery(id+"F0.wireOp",EDGE,"E8.17.1"),sQuery(id+"F0.wireOp",EDGE,"E8.17.2"),sQuery(id+"F0.wireOp",EDGE,"E8.17.3"),sQuery(id+"F0.wireOp",EDGE,"E8.17.4"),sQuery(id+"F0.wireOp",EDGE,"E8.17.5"),sQuery(id+"F0.wireOp",EDGE,"E8.18.0"),sQuery(id+"F0.wireOp",EDGE,"E8.18.1"),sQuery(id+"F0.wireOp",EDGE,"E8.18.2"),sQuery(id+"F0.wireOp",EDGE,"E8.18.3"),sQuery(id+"F0.wireOp",EDGE,"E8.18.4"),sQuery(id+"F0.wireOp",EDGE,"E8.18.5"),sQuery(id+"F0.wireOp",EDGE,"E8.19.0"),sQuery(id+"F0.wireOp",EDGE,"E8.19.1"),sQuery(id+"F0.wireOp",EDGE,"E8.19.2"),sQuery(id+"F0.wireOp",EDGE,"E8.19.3"),sQuery(id+"F0.wireOp",EDGE,"E8.19.4"),sQuery(id+"F0.wireOp",EDGE,"E8.19.5"),sQuery(id+"F0.wireOp",EDGE,"E8.20.0"),sQuery(id+"F0.wireOp",EDGE,"E8.20.1"),sQuery(id+"F0.wireOp",EDGE,"E8.20.2"),sQuery(id+"F0.wireOp",EDGE,"E8.20.3"),sQuery(id+"F0.wireOp",EDGE,"E8.20.4"),sQuery(id+"F0.wireOp",EDGE,"E8.20.5"),sQuery(id+"F0.wireOp",EDGE,"E8.21.0"),sQuery(id+"F0.wireOp",EDGE,"E8.21.1"),sQuery(id+"F0.wireOp",EDGE,"E8.21.2"),sQuery(id+"F0.wireOp",EDGE,"E8.21.3"),sQuery(id+"F0.wireOp",EDGE,"E8.21.4"),sQuery(id+"F0.wireOp",EDGE,"E8.21.5"),sQuery(id+"F0.wireOp",EDGE,"E8.22.0"),sQuery(id+"F0.wireOp",EDGE,"E8.22.1"),sQuery(id+"F0.wireOp",EDGE,"E8.22.2"),sQuery(id+"F0.wireOp",EDGE,"E8.22.3"),sQuery(id+"F0.wireOp",EDGE,"E8.22.4"),sQuery(id+"F0.wireOp",EDGE,"E8.22.5"),sQuery(id+"F0.wireOp",EDGE,"E8.23.0"),sQuery(id+"F0.wireOp",EDGE,"E8.23.1"),sQuery(id+"F0.wireOp",EDGE,"E8.23.2"),sQuery(id+"F0.wireOp",EDGE,"E8.23.3"),sQuery(id+"F0.wireOp",EDGE,"E8.23.4"),sQuery(id+"F0.wireOp",EDGE,"E8.23.5"),sQuery(id+"F0.wireOp",EDGE,"E8.24.0"),sQuery(id+"F0.wireOp",EDGE,"E8.24.1"),sQuery(id+"F0.wireOp",EDGE,"E8.24.2"),sQuery(id+"F0.wireOp",EDGE,"E8.24.3"),sQuery(id+"F0.wireOp",EDGE,"E8.24.4"),sQuery(id+"F0.wireOp",EDGE,"E8.24.5"),sQuery(id+"F0.wireOp",EDGE,"E8.25.0"),sQuery(id+"F0.wireOp",EDGE,"E8.25.1"),sQuery(id+"F0.wireOp",EDGE,"E8.25.2"),sQuery(id+"F0.wireOp",EDGE,"E8.25.3"),sQuery(id+"F0.wireOp",EDGE,"E8.25.4"),sQuery(id+"F0.wireOp",EDGE,"E8.25.5"),sQuery(id+"F0.wireOp",EDGE,"E8.26.0"),sQuery(id+"F0.wireOp",EDGE,"E8.26.1"),sQuery(id+"F0.wireOp",EDGE,"E8.26.2"),sQuery(id+"F0.wireOp",EDGE,"E8.26.3"),sQuery(id+"F0.wireOp",EDGE,"E8.26.4"),sQuery(id+"F0.wireOp",EDGE,"E8.26.5"),sQuery(id+"F0.wireOp",EDGE,"E8.27.0"),sQuery(id+"F0.wireOp",EDGE,"E8.27.1"),sQuery(id+"F0.wireOp",EDGE,"E8.27.2"),sQuery(id+"F0.wireOp",EDGE,"E8.27.3"),sQuery(id+"F0.wireOp",EDGE,"E8.27.4"),sQuery(id+"F0.wireOp",EDGE,"E8.27.5"),sQuery(id+"F0.wireOp",EDGE,"E8.28.0"),sQuery(id+"F0.wireOp",EDGE,"E8.28.1"),sQuery(id+"F0.wireOp",EDGE,"E8.28.2"),sQuery(id+"F0.wireOp",EDGE,"E8.28.3"),sQuery(id+"F0.wireOp",EDGE,"E8.28.4"),sQuery(id+"F0.wireOp",EDGE,"E8.28.5"),sQuery(id+"F0.wireOp",EDGE,"E8.29.0"),sQuery(id+"F0.wireOp",EDGE,"E8.29.1"),sQuery(id+"F0.wireOp",EDGE,"E8.29.2"),sQuery(id+"F0.wireOp",EDGE,"E8.29.3"),sQuery(id+"F0.wireOp",EDGE,"E8.29.4"),sQuery(id+"F0.wireOp",EDGE,"E8.29.5"),sQuery(id+"F0.wireOp",EDGE,"E8.30.0"),sQuery(id+"F0.wireOp",EDGE,"E8.30.1"),sQuery(id+"F0.wireOp",EDGE,"E8.30.2"),sQuery(id+"F0.wireOp",EDGE,"E8.30.3"),sQuery(id+"F0.wireOp",EDGE,"E8.30.4"),sQuery(id+"F0.wireOp",EDGE,"E8.30.5"),sQuery(id+"F0.wireOp",EDGE,"E8.31.0"),sQuery(id+"F0.wireOp",EDGE,"E8.31.1"),sQuery(id+"F0.wireOp",EDGE,"E8.31.2"),sQuery(id+"F0.wireOp",EDGE,"E8.31.3"),sQuery(id+"F0.wireOp",EDGE,"E8.31.4"),sQuery(id+"F0.wireOp",EDGE,"E8.31.5"),sQuery(id+"F0.wireOp",EDGE,"E8.32.0"),sQuery(id+"F0.wireOp",EDGE,"E8.32.1"),sQuery(id+"F0.wireOp",EDGE,"E8.32.2"),sQuery(id+"F0.wireOp",EDGE,"E8.32.3"),sQuery(id+"F0.wireOp",EDGE,"E8.32.4"),sQuery(id+"F0.wireOp",EDGE,"E8.32.5"),sQuery(id+"F0.wireOp",EDGE,"E8.33.0"),sQuery(id+"F0.wireOp",EDGE,"E8.33.1"),sQuery(id+"F0.wireOp",EDGE,"E8.33.2"),sQuery(id+"F0.wireOp",EDGE,"E8.33.3"),sQuery(id+"F0.wireOp",EDGE,"E8.33.4"),sQuery(id+"F0.wireOp",EDGE,"E8.33.5"),sQuery(id+"F0.wireOp",EDGE,"E8.34.0"),sQuery(id+"F0.wireOp",EDGE,"E8.34.1"),sQuery(id+"F0.wireOp",EDGE,"E8.34.2"),sQuery(id+"F0.wireOp",EDGE,"E8.34.3"),sQuery(id+"F0.wireOp",EDGE,"E8.34.4"),sQuery(id+"F0.wireOp",EDGE,"E8.34.5"),sQuery(id+"F0.wireOp",EDGE,"E8.35.0"),sQuery(id+"F0.wireOp",EDGE,"E8.35.1"),sQuery(id+"F0.wireOp",EDGE,"E8.35.2"),sQuery(id+"F0.wireOp",EDGE,"E8.35.3"),sQuery(id+"F0.wireOp",EDGE,"E8.35.4"),sQuery(id+"F0.wireOp",EDGE,"E8.35.5"),sQuery(id+"F0.wireOp",EDGE,"E8.36.0"),sQuery(id+"F0.wireOp",EDGE,"E8.36.1"),sQuery(id+"F0.wireOp",EDGE,"E8.36.2"),sQuery(id+"F0.wireOp",EDGE,"E8.36.3"),sQuery(id+"F0.wireOp",EDGE,"E8.36.4"),sQuery(id+"F0.wireOp",EDGE,"E8.36.5"),sQuery(id+"F0.wireOp",EDGE,"E8.37.0"),sQuery(id+"F0.wireOp",EDGE,"E8.37.1"),sQuery(id+"F0.wireOp",EDGE,"E8.37.2"),sQuery(id+"F0.wireOp",EDGE,"E8.37.3"),sQuery(id+"F0.wireOp",EDGE,"E8.37.4"),sQuery(id+"F0.wireOp",EDGE,"E8.37.5"),sQuery(id+"F0.wireOp",EDGE,"E8.38.0"),sQuery(id+"F0.wireOp",EDGE,"E8.38.1"),sQuery(id+"F0.wireOp",EDGE,"E8.38.2"),sQuery(id+"F0.wireOp",EDGE,"E8.38.3"),sQuery(id+"F0.wireOp",EDGE,"E8.38.4"),sQuery(id+"F0.wireOp",EDGE,"E8.38.5"),sQuery(id+"F0.wireOp",EDGE,"E8.39.0"),sQuery(id+"F0.wireOp",EDGE,"E8.39.1"),sQuery(id+"F0.wireOp",EDGE,"E8.39.2"),sQuery(id+"F0.wireOp",EDGE,"E8.39.3"),sQuery(id+"F0.wireOp",EDGE,"E8.39.4"),sQuery(id+"F0.wireOp",EDGE,"E8.39.5"),sQuery(id+"F0.wireOp",EDGE,"E8.40.0"),sQuery(id+"F0.wireOp",EDGE,"E8.40.1"),sQuery(id+"F0.wireOp",EDGE,"E8.40.2"),sQuery(id+"F0.wireOp",EDGE,"E8.40.3"),sQuery(id+"F0.wireOp",EDGE,"E8.40.4"),sQuery(id+"F0.wireOp",EDGE,"E8.40.5"),sQuery(id+"F0.wireOp",EDGE,"E8.41.0"),sQuery(id+"F0.wireOp",EDGE,"E8.41.1"),sQuery(id+"F0.wireOp",EDGE,"E8.41.2"),sQuery(id+"F0.wireOp",EDGE,"E8.41.3"),sQuery(id+"F0.wireOp",EDGE,"E8.41.4"),sQuery(id+"F0.wireOp",EDGE,"E8.41.5"),sQuery(id+"F0.wireOp",EDGE,"E8.42.0"),sQuery(id+"F0.wireOp",EDGE,"E8.42.1"),sQuery(id+"F0.wireOp",EDGE,"E8.42.2"),sQuery(id+"F0.wireOp",EDGE,"E8.42.3"),sQuery(id+"F0.wireOp",EDGE,"E8.42.4"),sQuery(id+"F0.wireOp",EDGE,"E8.42.5"),sQuery(id+"F0.wireOp",EDGE,"E8.43.0"),sQuery(id+"F0.wireOp",EDGE,"E8.43.1"),sQuery(id+"F0.wireOp",EDGE,"E8.43.2"),sQuery(id+"F0.wireOp",EDGE,"E8.43.3"),sQuery(id+"F0.wireOp",EDGE,"E8.43.4"),sQuery(id+"F0.wireOp",EDGE,"E8.43.5"),sQuery(id+"F0.wireOp",EDGE,"E8.44.0"),sQuery(id+"F0.wireOp",EDGE,"E8.44.1"),sQuery(id+"F0.wireOp",EDGE,"E8.44.2"),sQuery(id+"F0.wireOp",EDGE,"E8.44.3"),sQuery(id+"F0.wireOp",EDGE,"E8.44.4"),sQuery(id+"F0.wireOp",EDGE,"E8.44.5"),sQuery(id+"F0.wireOp",EDGE,"E8.45.0"),sQuery(id+"F0.wireOp",EDGE,"E8.45.1"),sQuery(id+"F0.wireOp",EDGE,"E8.45.2"),sQuery(id+"F0.wireOp",EDGE,"E8.45.3"),sQuery(id+"F0.wireOp",EDGE,"E8.45.4"),sQuery(id+"F0.wireOp",EDGE,"E8.45.5"),sQuery(id+"F0.wireOp",EDGE,"E8.46.0"),sQuery(id+"F0.wireOp",EDGE,"E8.46.1"),sQuery(id+"F0.wireOp",EDGE,"E8.46.2"),sQuery(id+"F0.wireOp",EDGE,"E8.46.3"),sQuery(id+"F0.wireOp",EDGE,"E8.46.4"),sQuery(id+"F0.wireOp",EDGE,"E8.46.5"),sQuery(id+"F0.wireOp",EDGE,"E8.47.0"),sQuery(id+"F0.wireOp",EDGE,"E8.47.1"),sQuery(id+"F0.wireOp",EDGE,"E8.47.2"),sQuery(id+"F0.wireOp",EDGE,"E8.47.3"),sQuery(id+"F0.wireOp",EDGE,"E8.47.4"),sQuery(id+"F0.wireOp",EDGE,"E8.47.5"),sQuery(id+"F0.wireOp",EDGE,"E8.48.0"),sQuery(id+"F0.wireOp",EDGE,"E8.48.1"),sQuery(id+"F0.wireOp",EDGE,"E8.48.2"),sQuery(id+"F0.wireOp",EDGE,"E8.48.3"),sQuery(id+"F0.wireOp",EDGE,"E8.48.4"),sQuery(id+"F0.wireOp",EDGE,"E8.48.5"),sQuery(id+"F0.wireOp",EDGE,"E8.49.0"),sQuery(id+"F0.wireOp",EDGE,"E8.49.1"),sQuery(id+"F0.wireOp",EDGE,"E8.49.2"),sQuery(id+"F0.wireOp",EDGE,"E8.49.3"),sQuery(id+"F0.wireOp",EDGE,"E8.49.4"),sQuery(id+"F0.wireOp",EDGE,"E8.49.5"),sQuery(id+"F0.wireOp",EDGE,"E8.50.0"),sQuery(id+"F0.wireOp",EDGE,"E8.50.1"),sQuery(id+"F0.wireOp",EDGE,"E8.50.2"),sQuery(id+"F0.wireOp",EDGE,"E8.50.3"),sQuery(id+"F0.wireOp",EDGE,"E8.50.4"),sQuery(id+"F0.wireOp",EDGE,"E8.50.5"),sQuery(id+"F0.wireOp",EDGE,"E8.51.0"),sQuery(id+"F0.wireOp",EDGE,"E8.51.1"),sQuery(id+"F0.wireOp",EDGE,"E8.51.2"),sQuery(id+"F0.wireOp",EDGE,"E8.51.3"),sQuery(id+"F0.wireOp",EDGE,"E8.51.4"),sQuery(id+"F0.wireOp",EDGE,"E8.51.5"),sQuery(id+"F0.wireOp",EDGE,"E8.52.0"),sQuery(id+"F0.wireOp",EDGE,"E8.52.1"),sQuery(id+"F0.wireOp",EDGE,"E8.52.2"),sQuery(id+"F0.wireOp",EDGE,"E8.52.3"),sQuery(id+"F0.wireOp",EDGE,"E8.52.4"),sQuery(id+"F0.wireOp",EDGE,"E8.52.5"),sQuery(id+"F0.wireOp",EDGE,"E8.53.0"),sQuery(id+"F0.wireOp",EDGE,"E8.53.1"),sQuery(id+"F0.wireOp",EDGE,"E8.53.2"),sQuery(id+"F0.wireOp",EDGE,"E8.53.3"),sQuery(id+"F0.wireOp",EDGE,"E8.53.4"),sQuery(id+"F0.wireOp",EDGE,"E8.53.5"),sQuery(id+"F0.wireOp",EDGE,"E8.54.0"),sQuery(id+"F0.wireOp",EDGE,"E8.54.1"),sQuery(id+"F0.wireOp",EDGE,"E8.54.2"),sQuery(id+"F0.wireOp",EDGE,"E8.54.3"),sQuery(id+"F0.wireOp",EDGE,"E8.54.4"),sQuery(id+"F0.wireOp",EDGE,"E8.54.5"),sQuery(id+"F0.wireOp",EDGE,"E8.55.0"),sQuery(id+"F0.wireOp",EDGE,"E8.55.1"),sQuery(id+"F0.wireOp",EDGE,"E8.55.2"),sQuery(id+"F0.wireOp",EDGE,"E8.55.3"),sQuery(id+"F0.wireOp",EDGE,"E8.55.4"),sQuery(id+"F0.wireOp",EDGE,"E8.55.5"),sQuery(id+"F0.wireOp",EDGE,"E8.56.0"),sQuery(id+"F0.wireOp",EDGE,"E8.56.1"),sQuery(id+"F0.wireOp",EDGE,"E8.56.2"),sQuery(id+"F0.wireOp",EDGE,"E8.56.3"),sQuery(id+"F0.wireOp",EDGE,"E8.56.4"),sQuery(id+"F0.wireOp",EDGE,"E8.56.5"),sQuery(id+"F0.wireOp",EDGE,"E8.57.0"),sQuery(id+"F0.wireOp",EDGE,"E8.57.1"),sQuery(id+"F0.wireOp",EDGE,"E8.57.2"),sQuery(id+"F0.wireOp",EDGE,"E8.57.3"),sQuery(id+"F0.wireOp",EDGE,"E8.57.4"),sQuery(id+"F0.wireOp",EDGE,"E8.57.5"),sQuery(id+"F0.wireOp",EDGE,"E8.58.0"),sQuery(id+"F0.wireOp",EDGE,"E8.58.1"),sQuery(id+"F0.wireOp",EDGE,"E8.58.2"),sQuery(id+"F0.wireOp",EDGE,"E8.58.3"),sQuery(id+"F0.wireOp",EDGE,"E8.58.4"),sQuery(id+"F0.wireOp",EDGE,"E8.58.5"),sQuery(id+"F0.wireOp",EDGE,"E8.59.0"),sQuery(id+"F0.wireOp",EDGE,"E8.59.1"),sQuery(id+"F0.wireOp",EDGE,"E8.59.2"),sQuery(id+"F0.wireOp",EDGE,"E8.59.3"),sQuery(id+"F0.wireOp",EDGE,"E8.59.4"),sQuery(id+"F0.wireOp",EDGE,"E8.59.5"),sQuery(id+"F0.wireOp",EDGE,"E8.60.0"),sQuery(id+"F0.wireOp",EDGE,"E8.60.1"),sQuery(id+"F0.wireOp",EDGE,"E8.60.2"),sQuery(id+"F0.wireOp",EDGE,"E8.60.3"),sQuery(id+"F0.wireOp",EDGE,"E8.60.4"),sQuery(id+"F0.wireOp",EDGE,"E8.60.5"),sQuery(id+"F0.wireOp",EDGE,"E8.61.0"),sQuery(id+"F0.wireOp",EDGE,"E8.61.1"),sQuery(id+"F0.wireOp",EDGE,"E8.61.2"),sQuery(id+"F0.wireOp",EDGE,"E8.61.3"),sQuery(id+"F0.wireOp",EDGE,"E8.61.4"),sQuery(id+"F0.wireOp",EDGE,"E8.61.5"),sQuery(id+"F0.wireOp",EDGE,"E8.62.0"),sQuery(id+"F0.wireOp",EDGE,"E8.62.1"),sQuery(id+"F0.wireOp",EDGE,"E8.62.2"),sQuery(id+"F0.wireOp",EDGE,"E8.62.3"),sQuery(id+"F0.wireOp",EDGE,"E8.62.4"),sQuery(id+"F0.wireOp",EDGE,"E8.62.5"),sQuery(id+"F0.wireOp",EDGE,"E8.63.0"),sQuery(id+"F0.wireOp",EDGE,"E8.63.1"),sQuery(id+"F0.wireOp",EDGE,"E8.63.2"),sQuery(id+"F0.wireOp",EDGE,"E8.63.3"),sQuery(id+"F0.wireOp",EDGE,"E8.63.4"),sQuery(id+"F0.wireOp",EDGE,"E8.63.5"),sQuery(id+"F0.wireOp",EDGE,"E8.64.0"),sQuery(id+"F0.wireOp",EDGE,"E8.64.1"),sQuery(id+"F0.wireOp",EDGE,"E8.64.2"),sQuery(id+"F0.wireOp",EDGE,"E8.64.3"),sQuery(id+"F0.wireOp",EDGE,"E8.64.4"),sQuery(id+"F0.wireOp",EDGE,"E8.64.5"),sQuery(id+"F0.wireOp",EDGE,"E8.65.0"),sQuery(id+"F0.wireOp",EDGE,"E8.65.1"),sQuery(id+"F0.wireOp",EDGE,"E8.65.2"),sQuery(id+"F0.wireOp",EDGE,"E8.65.3"),sQuery(id+"F0.wireOp",EDGE,"E8.65.4"),sQuery(id+"F0.wireOp",EDGE,"E8.65.5"),sQuery(id+"F0.wireOp",EDGE,"E8.66.0"),sQuery(id+"F0.wireOp",EDGE,"E8.66.1"),sQuery(id+"F0.wireOp",EDGE,"E8.66.2"),sQuery(id+"F0.wireOp",EDGE,"E8.66.3"),sQuery(id+"F0.wireOp",EDGE,"E8.66.4"),sQuery(id+"F0.wireOp",EDGE,"E8.66.5"),sQuery(id+"F0.wireOp",EDGE,"E8.67.0"),sQuery(id+"F0.wireOp",EDGE,"E8.67.1"),sQuery(id+"F0.wireOp",EDGE,"E8.67.2"),sQuery(id+"F0.wireOp",EDGE,"E8.67.3"),sQuery(id+"F0.wireOp",EDGE,"E8.67.4"),sQuery(id+"F0.wireOp",EDGE,"E8.67.5"),sQuery(id+"F0.wireOp",EDGE,"E8.68.0"),sQuery(id+"F0.wireOp",EDGE,"E8.68.1"),sQuery(id+"F0.wireOp",EDGE,"E8.68.2"),sQuery(id+"F0.wireOp",EDGE,"E8.68.3"),sQuery(id+"F0.wireOp",EDGE,"E8.68.4"),sQuery(id+"F0.wireOp",EDGE,"E8.68.5"),sQuery(id+"F0.wireOp",EDGE,"E8.69.0"),sQuery(id+"F0.wireOp",EDGE,"E8.69.1"),sQuery(id+"F0.wireOp",EDGE,"E8.69.2"),sQuery(id+"F0.wireOp",EDGE,"E8.69.3"),sQuery(id+"F0.wireOp",EDGE,"E8.69.4"),sQuery(id+"F0.wireOp",EDGE,"E8.69.5"),sQuery(id+"F0.wireOp",EDGE,"E8.70.0"),sQuery(id+"F0.wireOp",EDGE,"E8.70.1"),sQuery(id+"F0.wireOp",EDGE,"E8.70.2"),sQuery(id+"F0.wireOp",EDGE,"E8.70.3"),sQuery(id+"F0.wireOp",EDGE,"E8.70.4"),sQuery(id+"F0.wireOp",EDGE,"E8.70.5"),sQuery(id+"F0.wireOp",EDGE,"E8.71.0"),sQuery(id+"F0.wireOp",EDGE,"E8.71.1"),sQuery(id+"F0.wireOp",EDGE,"E8.71.2"),sQuery(id+"F0.wireOp",EDGE,"E8.71.3"),sQuery(id+"F0.wireOp",EDGE,"E8.71.4"),sQuery(id+"F0.wireOp",EDGE,"E8.71.5"),sQuery(id+"F0.wireOp",EDGE,"E9")])],"isStart":false});
            var sketch = newSketch(context, id + "F2", { "sketchPlane" : qUnion([Q0])});
            skCircle(sketch, "E10.0", {"center": v(0, 0) * mm, "radius": 84.67 * mm});
            skSolve(sketch);
        }
        {
            var Q0;
            Q0 = qSketchRegion(id + "F2", true);
            extrude(context, id + "F3", {"entities" : qUnion([Q0]), "operationType" : NewBodyOperationType.ADD, "depth" : 6.35 * mm});
        }
        {
            var Q0;
            Q0=makeQuery(id+"F3.opExtrude","CAP_FACE",FACE,{"disambiguationData":[OSD([sQuery(id+"F2.wireOp",EDGE,"E10.0")])],"isStart":true});
            var sketch = newSketch(context, id + "F4", { "sketchPlane" : qUnion([Q0])});
            skPoint(sketch, "E11", {"position": v(0, 50.15) * mm});
            skPoint(sketch, "E12.1.0", {"position": v(-44, -26.86) * mm});
            skPoint(sketch, "E12.2.0", {"position": v(43.33, -26.48) * mm});
            skPoint(sketch, "E12.center", {"position": v(0, -1.46) * mm});
            skSolve(sketch);
        }
        {
            var Q0;
            Q0=sQuery(id+"F4.wireOp",VERTEX,"E12.1.0");
            var Q1;
            Q1=sQuery(id+"F4.wireOp",VERTEX,"E12.2.0");
            var Q2;
            Q2=sQuery(id+"F4.wireOp",VERTEX,"E11");
            var Q3;
            Q3=makeQuery(id+"F1.opExtrude","SWEPT_BODY",BODY,{"disambiguationData":[OSD([sQuery(id+"F0.wireOp",EDGE,"E0"),sQuery(id+"F0.wireOp",EDGE,"E2.trimOffspring"),sQuery(id+"F0.wireOp",EDGE,"E3"),sQuery(id+"F0.wireOp",EDGE,"E4"),sQuery(id+"F0.wireOp",EDGE,"E5.MirrorCS"),sQuery(id+"F0.wireOp",EDGE,"E6.MirrorCS"),sQuery(id+"F0.wireOp",EDGE,"E7.MirrorCS"),sQuery(id+"F0.wireOp",EDGE,"E8.1.0"),sQuery(id+"F0.wireOp",EDGE,"E8.1.1"),sQuery(id+"F0.wireOp",EDGE,"E8.1.2"),sQuery(id+"F0.wireOp",EDGE,"E8.1.3"),sQuery(id+"F0.wireOp",EDGE,"E8.1.4"),sQuery(id+"F0.wireOp",EDGE,"E8.1.5"),sQuery(id+"F0.wireOp",EDGE,"E8.2.0"),sQuery(id+"F0.wireOp",EDGE,"E8.2.1"),sQuery(id+"F0.wireOp",EDGE,"E8.2.2"),sQuery(id+"F0.wireOp",EDGE,"E8.2.3"),sQuery(id+"F0.wireOp",EDGE,"E8.2.4"),sQuery(id+"F0.wireOp",EDGE,"E8.2.5"),sQuery(id+"F0.wireOp",EDGE,"E8.3.0"),sQuery(id+"F0.wireOp",EDGE,"E8.3.1"),sQuery(id+"F0.wireOp",EDGE,"E8.3.2"),sQuery(id+"F0.wireOp",EDGE,"E8.3.3"),sQuery(id+"F0.wireOp",EDGE,"E8.3.4"),sQuery(id+"F0.wireOp",EDGE,"E8.3.5"),sQuery(id+"F0.wireOp",EDGE,"E8.4.0"),sQuery(id+"F0.wireOp",EDGE,"E8.4.1"),sQuery(id+"F0.wireOp",EDGE,"E8.4.2"),sQuery(id+"F0.wireOp",EDGE,"E8.4.3"),sQuery(id+"F0.wireOp",EDGE,"E8.4.4"),sQuery(id+"F0.wireOp",EDGE,"E8.4.5"),sQuery(id+"F0.wireOp",EDGE,"E8.5.0"),sQuery(id+"F0.wireOp",EDGE,"E8.5.1"),sQuery(id+"F0.wireOp",EDGE,"E8.5.2"),sQuery(id+"F0.wireOp",EDGE,"E8.5.3"),sQuery(id+"F0.wireOp",EDGE,"E8.5.4"),sQuery(id+"F0.wireOp",EDGE,"E8.5.5"),sQuery(id+"F0.wireOp",EDGE,"E8.6.0"),sQuery(id+"F0.wireOp",EDGE,"E8.6.1"),sQuery(id+"F0.wireOp",EDGE,"E8.6.2"),sQuery(id+"F0.wireOp",EDGE,"E8.6.3"),sQuery(id+"F0.wireOp",EDGE,"E8.6.4"),sQuery(id+"F0.wireOp",EDGE,"E8.6.5"),sQuery(id+"F0.wireOp",EDGE,"E8.7.0"),sQuery(id+"F0.wireOp",EDGE,"E8.7.1"),sQuery(id+"F0.wireOp",EDGE,"E8.7.2"),sQuery(id+"F0.wireOp",EDGE,"E8.7.3"),sQuery(id+"F0.wireOp",EDGE,"E8.7.4"),sQuery(id+"F0.wireOp",EDGE,"E8.7.5"),sQuery(id+"F0.wireOp",EDGE,"E8.8.0"),sQuery(id+"F0.wireOp",EDGE,"E8.8.1"),sQuery(id+"F0.wireOp",EDGE,"E8.8.2"),sQuery(id+"F0.wireOp",EDGE,"E8.8.3"),sQuery(id+"F0.wireOp",EDGE,"E8.8.4"),sQuery(id+"F0.wireOp",EDGE,"E8.8.5"),sQuery(id+"F0.wireOp",EDGE,"E8.9.0"),sQuery(id+"F0.wireOp",EDGE,"E8.9.1"),sQuery(id+"F0.wireOp",EDGE,"E8.9.2"),sQuery(id+"F0.wireOp",EDGE,"E8.9.3"),sQuery(id+"F0.wireOp",EDGE,"E8.9.4"),sQuery(id+"F0.wireOp",EDGE,"E8.9.5"),sQuery(id+"F0.wireOp",EDGE,"E8.10.0"),sQuery(id+"F0.wireOp",EDGE,"E8.10.1"),sQuery(id+"F0.wireOp",EDGE,"E8.10.2"),sQuery(id+"F0.wireOp",EDGE,"E8.10.3"),sQuery(id+"F0.wireOp",EDGE,"E8.10.4"),sQuery(id+"F0.wireOp",EDGE,"E8.10.5"),sQuery(id+"F0.wireOp",EDGE,"E8.11.0"),sQuery(id+"F0.wireOp",EDGE,"E8.11.1"),sQuery(id+"F0.wireOp",EDGE,"E8.11.2"),sQuery(id+"F0.wireOp",EDGE,"E8.11.3"),sQuery(id+"F0.wireOp",EDGE,"E8.11.4"),sQuery(id+"F0.wireOp",EDGE,"E8.11.5"),sQuery(id+"F0.wireOp",EDGE,"E8.12.0"),sQuery(id+"F0.wireOp",EDGE,"E8.12.1"),sQuery(id+"F0.wireOp",EDGE,"E8.12.2"),sQuery(id+"F0.wireOp",EDGE,"E8.12.3"),sQuery(id+"F0.wireOp",EDGE,"E8.12.4"),sQuery(id+"F0.wireOp",EDGE,"E8.12.5"),sQuery(id+"F0.wireOp",EDGE,"E8.13.0"),sQuery(id+"F0.wireOp",EDGE,"E8.13.1"),sQuery(id+"F0.wireOp",EDGE,"E8.13.2"),sQuery(id+"F0.wireOp",EDGE,"E8.13.3"),sQuery(id+"F0.wireOp",EDGE,"E8.13.4"),sQuery(id+"F0.wireOp",EDGE,"E8.13.5"),sQuery(id+"F0.wireOp",EDGE,"E8.14.0"),sQuery(id+"F0.wireOp",EDGE,"E8.14.1"),sQuery(id+"F0.wireOp",EDGE,"E8.14.2"),sQuery(id+"F0.wireOp",EDGE,"E8.14.3"),sQuery(id+"F0.wireOp",EDGE,"E8.14.4"),sQuery(id+"F0.wireOp",EDGE,"E8.14.5"),sQuery(id+"F0.wireOp",EDGE,"E8.15.0"),sQuery(id+"F0.wireOp",EDGE,"E8.15.1"),sQuery(id+"F0.wireOp",EDGE,"E8.15.2"),sQuery(id+"F0.wireOp",EDGE,"E8.15.3"),sQuery(id+"F0.wireOp",EDGE,"E8.15.4"),sQuery(id+"F0.wireOp",EDGE,"E8.15.5"),sQuery(id+"F0.wireOp",EDGE,"E8.16.0"),sQuery(id+"F0.wireOp",EDGE,"E8.16.1"),sQuery(id+"F0.wireOp",EDGE,"E8.16.2"),sQuery(id+"F0.wireOp",EDGE,"E8.16.3"),sQuery(id+"F0.wireOp",EDGE,"E8.16.4"),sQuery(id+"F0.wireOp",EDGE,"E8.16.5"),sQuery(id+"F0.wireOp",EDGE,"E8.17.0"),sQuery(id+"F0.wireOp",EDGE,"E8.17.1"),sQuery(id+"F0.wireOp",EDGE,"E8.17.2"),sQuery(id+"F0.wireOp",EDGE,"E8.17.3"),sQuery(id+"F0.wireOp",EDGE,"E8.17.4"),sQuery(id+"F0.wireOp",EDGE,"E8.17.5"),sQuery(id+"F0.wireOp",EDGE,"E8.18.0"),sQuery(id+"F0.wireOp",EDGE,"E8.18.1"),sQuery(id+"F0.wireOp",EDGE,"E8.18.2"),sQuery(id+"F0.wireOp",EDGE,"E8.18.3"),sQuery(id+"F0.wireOp",EDGE,"E8.18.4"),sQuery(id+"F0.wireOp",EDGE,"E8.18.5"),sQuery(id+"F0.wireOp",EDGE,"E8.19.0"),sQuery(id+"F0.wireOp",EDGE,"E8.19.1"),sQuery(id+"F0.wireOp",EDGE,"E8.19.2"),sQuery(id+"F0.wireOp",EDGE,"E8.19.3"),sQuery(id+"F0.wireOp",EDGE,"E8.19.4"),sQuery(id+"F0.wireOp",EDGE,"E8.19.5"),sQuery(id+"F0.wireOp",EDGE,"E8.20.0"),sQuery(id+"F0.wireOp",EDGE,"E8.20.1"),sQuery(id+"F0.wireOp",EDGE,"E8.20.2"),sQuery(id+"F0.wireOp",EDGE,"E8.20.3"),sQuery(id+"F0.wireOp",EDGE,"E8.20.4"),sQuery(id+"F0.wireOp",EDGE,"E8.20.5"),sQuery(id+"F0.wireOp",EDGE,"E8.21.0"),sQuery(id+"F0.wireOp",EDGE,"E8.21.1"),sQuery(id+"F0.wireOp",EDGE,"E8.21.2"),sQuery(id+"F0.wireOp",EDGE,"E8.21.3"),sQuery(id+"F0.wireOp",EDGE,"E8.21.4"),sQuery(id+"F0.wireOp",EDGE,"E8.21.5"),sQuery(id+"F0.wireOp",EDGE,"E8.22.0"),sQuery(id+"F0.wireOp",EDGE,"E8.22.1"),sQuery(id+"F0.wireOp",EDGE,"E8.22.2"),sQuery(id+"F0.wireOp",EDGE,"E8.22.3"),sQuery(id+"F0.wireOp",EDGE,"E8.22.4"),sQuery(id+"F0.wireOp",EDGE,"E8.22.5"),sQuery(id+"F0.wireOp",EDGE,"E8.23.0"),sQuery(id+"F0.wireOp",EDGE,"E8.23.1"),sQuery(id+"F0.wireOp",EDGE,"E8.23.2"),sQuery(id+"F0.wireOp",EDGE,"E8.23.3"),sQuery(id+"F0.wireOp",EDGE,"E8.23.4"),sQuery(id+"F0.wireOp",EDGE,"E8.23.5"),sQuery(id+"F0.wireOp",EDGE,"E8.24.0"),sQuery(id+"F0.wireOp",EDGE,"E8.24.1"),sQuery(id+"F0.wireOp",EDGE,"E8.24.2"),sQuery(id+"F0.wireOp",EDGE,"E8.24.3"),sQuery(id+"F0.wireOp",EDGE,"E8.24.4"),sQuery(id+"F0.wireOp",EDGE,"E8.24.5"),sQuery(id+"F0.wireOp",EDGE,"E8.25.0"),sQuery(id+"F0.wireOp",EDGE,"E8.25.1"),sQuery(id+"F0.wireOp",EDGE,"E8.25.2"),sQuery(id+"F0.wireOp",EDGE,"E8.25.3"),sQuery(id+"F0.wireOp",EDGE,"E8.25.4"),sQuery(id+"F0.wireOp",EDGE,"E8.25.5"),sQuery(id+"F0.wireOp",EDGE,"E8.26.0"),sQuery(id+"F0.wireOp",EDGE,"E8.26.1"),sQuery(id+"F0.wireOp",EDGE,"E8.26.2"),sQuery(id+"F0.wireOp",EDGE,"E8.26.3"),sQuery(id+"F0.wireOp",EDGE,"E8.26.4"),sQuery(id+"F0.wireOp",EDGE,"E8.26.5"),sQuery(id+"F0.wireOp",EDGE,"E8.27.0"),sQuery(id+"F0.wireOp",EDGE,"E8.27.1"),sQuery(id+"F0.wireOp",EDGE,"E8.27.2"),sQuery(id+"F0.wireOp",EDGE,"E8.27.3"),sQuery(id+"F0.wireOp",EDGE,"E8.27.4"),sQuery(id+"F0.wireOp",EDGE,"E8.27.5"),sQuery(id+"F0.wireOp",EDGE,"E8.28.0"),sQuery(id+"F0.wireOp",EDGE,"E8.28.1"),sQuery(id+"F0.wireOp",EDGE,"E8.28.2"),sQuery(id+"F0.wireOp",EDGE,"E8.28.3"),sQuery(id+"F0.wireOp",EDGE,"E8.28.4"),sQuery(id+"F0.wireOp",EDGE,"E8.28.5"),sQuery(id+"F0.wireOp",EDGE,"E8.29.0"),sQuery(id+"F0.wireOp",EDGE,"E8.29.1"),sQuery(id+"F0.wireOp",EDGE,"E8.29.2"),sQuery(id+"F0.wireOp",EDGE,"E8.29.3"),sQuery(id+"F0.wireOp",EDGE,"E8.29.4"),sQuery(id+"F0.wireOp",EDGE,"E8.29.5"),sQuery(id+"F0.wireOp",EDGE,"E8.30.0"),sQuery(id+"F0.wireOp",EDGE,"E8.30.1"),sQuery(id+"F0.wireOp",EDGE,"E8.30.2"),sQuery(id+"F0.wireOp",EDGE,"E8.30.3"),sQuery(id+"F0.wireOp",EDGE,"E8.30.4"),sQuery(id+"F0.wireOp",EDGE,"E8.30.5"),sQuery(id+"F0.wireOp",EDGE,"E8.31.0"),sQuery(id+"F0.wireOp",EDGE,"E8.31.1"),sQuery(id+"F0.wireOp",EDGE,"E8.31.2"),sQuery(id+"F0.wireOp",EDGE,"E8.31.3"),sQuery(id+"F0.wireOp",EDGE,"E8.31.4"),sQuery(id+"F0.wireOp",EDGE,"E8.31.5"),sQuery(id+"F0.wireOp",EDGE,"E8.32.0"),sQuery(id+"F0.wireOp",EDGE,"E8.32.1"),sQuery(id+"F0.wireOp",EDGE,"E8.32.2"),sQuery(id+"F0.wireOp",EDGE,"E8.32.3"),sQuery(id+"F0.wireOp",EDGE,"E8.32.4"),sQuery(id+"F0.wireOp",EDGE,"E8.32.5"),sQuery(id+"F0.wireOp",EDGE,"E8.33.0"),sQuery(id+"F0.wireOp",EDGE,"E8.33.1"),sQuery(id+"F0.wireOp",EDGE,"E8.33.2"),sQuery(id+"F0.wireOp",EDGE,"E8.33.3"),sQuery(id+"F0.wireOp",EDGE,"E8.33.4"),sQuery(id+"F0.wireOp",EDGE,"E8.33.5"),sQuery(id+"F0.wireOp",EDGE,"E8.34.0"),sQuery(id+"F0.wireOp",EDGE,"E8.34.1"),sQuery(id+"F0.wireOp",EDGE,"E8.34.2"),sQuery(id+"F0.wireOp",EDGE,"E8.34.3"),sQuery(id+"F0.wireOp",EDGE,"E8.34.4"),sQuery(id+"F0.wireOp",EDGE,"E8.34.5"),sQuery(id+"F0.wireOp",EDGE,"E8.35.0"),sQuery(id+"F0.wireOp",EDGE,"E8.35.1"),sQuery(id+"F0.wireOp",EDGE,"E8.35.2"),sQuery(id+"F0.wireOp",EDGE,"E8.35.3"),sQuery(id+"F0.wireOp",EDGE,"E8.35.4"),sQuery(id+"F0.wireOp",EDGE,"E8.35.5"),sQuery(id+"F0.wireOp",EDGE,"E8.36.0"),sQuery(id+"F0.wireOp",EDGE,"E8.36.1"),sQuery(id+"F0.wireOp",EDGE,"E8.36.2"),sQuery(id+"F0.wireOp",EDGE,"E8.36.3"),sQuery(id+"F0.wireOp",EDGE,"E8.36.4"),sQuery(id+"F0.wireOp",EDGE,"E8.36.5"),sQuery(id+"F0.wireOp",EDGE,"E8.37.0"),sQuery(id+"F0.wireOp",EDGE,"E8.37.1"),sQuery(id+"F0.wireOp",EDGE,"E8.37.2"),sQuery(id+"F0.wireOp",EDGE,"E8.37.3"),sQuery(id+"F0.wireOp",EDGE,"E8.37.4"),sQuery(id+"F0.wireOp",EDGE,"E8.37.5"),sQuery(id+"F0.wireOp",EDGE,"E8.38.0"),sQuery(id+"F0.wireOp",EDGE,"E8.38.1"),sQuery(id+"F0.wireOp",EDGE,"E8.38.2"),sQuery(id+"F0.wireOp",EDGE,"E8.38.3"),sQuery(id+"F0.wireOp",EDGE,"E8.38.4"),sQuery(id+"F0.wireOp",EDGE,"E8.38.5"),sQuery(id+"F0.wireOp",EDGE,"E8.39.0"),sQuery(id+"F0.wireOp",EDGE,"E8.39.1"),sQuery(id+"F0.wireOp",EDGE,"E8.39.2"),sQuery(id+"F0.wireOp",EDGE,"E8.39.3"),sQuery(id+"F0.wireOp",EDGE,"E8.39.4"),sQuery(id+"F0.wireOp",EDGE,"E8.39.5"),sQuery(id+"F0.wireOp",EDGE,"E8.40.0"),sQuery(id+"F0.wireOp",EDGE,"E8.40.1"),sQuery(id+"F0.wireOp",EDGE,"E8.40.2"),sQuery(id+"F0.wireOp",EDGE,"E8.40.3"),sQuery(id+"F0.wireOp",EDGE,"E8.40.4"),sQuery(id+"F0.wireOp",EDGE,"E8.40.5"),sQuery(id+"F0.wireOp",EDGE,"E8.41.0"),sQuery(id+"F0.wireOp",EDGE,"E8.41.1"),sQuery(id+"F0.wireOp",EDGE,"E8.41.2"),sQuery(id+"F0.wireOp",EDGE,"E8.41.3"),sQuery(id+"F0.wireOp",EDGE,"E8.41.4"),sQuery(id+"F0.wireOp",EDGE,"E8.41.5"),sQuery(id+"F0.wireOp",EDGE,"E8.42.0"),sQuery(id+"F0.wireOp",EDGE,"E8.42.1"),sQuery(id+"F0.wireOp",EDGE,"E8.42.2"),sQuery(id+"F0.wireOp",EDGE,"E8.42.3"),sQuery(id+"F0.wireOp",EDGE,"E8.42.4"),sQuery(id+"F0.wireOp",EDGE,"E8.42.5"),sQuery(id+"F0.wireOp",EDGE,"E8.43.0"),sQuery(id+"F0.wireOp",EDGE,"E8.43.1"),sQuery(id+"F0.wireOp",EDGE,"E8.43.2"),sQuery(id+"F0.wireOp",EDGE,"E8.43.3"),sQuery(id+"F0.wireOp",EDGE,"E8.43.4"),sQuery(id+"F0.wireOp",EDGE,"E8.43.5"),sQuery(id+"F0.wireOp",EDGE,"E8.44.0"),sQuery(id+"F0.wireOp",EDGE,"E8.44.1"),sQuery(id+"F0.wireOp",EDGE,"E8.44.2"),sQuery(id+"F0.wireOp",EDGE,"E8.44.3"),sQuery(id+"F0.wireOp",EDGE,"E8.44.4"),sQuery(id+"F0.wireOp",EDGE,"E8.44.5"),sQuery(id+"F0.wireOp",EDGE,"E8.45.0"),sQuery(id+"F0.wireOp",EDGE,"E8.45.1"),sQuery(id+"F0.wireOp",EDGE,"E8.45.2"),sQuery(id+"F0.wireOp",EDGE,"E8.45.3"),sQuery(id+"F0.wireOp",EDGE,"E8.45.4"),sQuery(id+"F0.wireOp",EDGE,"E8.45.5"),sQuery(id+"F0.wireOp",EDGE,"E8.46.0"),sQuery(id+"F0.wireOp",EDGE,"E8.46.1"),sQuery(id+"F0.wireOp",EDGE,"E8.46.2"),sQuery(id+"F0.wireOp",EDGE,"E8.46.3"),sQuery(id+"F0.wireOp",EDGE,"E8.46.4"),sQuery(id+"F0.wireOp",EDGE,"E8.46.5"),sQuery(id+"F0.wireOp",EDGE,"E8.47.0"),sQuery(id+"F0.wireOp",EDGE,"E8.47.1"),sQuery(id+"F0.wireOp",EDGE,"E8.47.2"),sQuery(id+"F0.wireOp",EDGE,"E8.47.3"),sQuery(id+"F0.wireOp",EDGE,"E8.47.4"),sQuery(id+"F0.wireOp",EDGE,"E8.47.5"),sQuery(id+"F0.wireOp",EDGE,"E8.48.0"),sQuery(id+"F0.wireOp",EDGE,"E8.48.1"),sQuery(id+"F0.wireOp",EDGE,"E8.48.2"),sQuery(id+"F0.wireOp",EDGE,"E8.48.3"),sQuery(id+"F0.wireOp",EDGE,"E8.48.4"),sQuery(id+"F0.wireOp",EDGE,"E8.48.5"),sQuery(id+"F0.wireOp",EDGE,"E8.49.0"),sQuery(id+"F0.wireOp",EDGE,"E8.49.1"),sQuery(id+"F0.wireOp",EDGE,"E8.49.2"),sQuery(id+"F0.wireOp",EDGE,"E8.49.3"),sQuery(id+"F0.wireOp",EDGE,"E8.49.4"),sQuery(id+"F0.wireOp",EDGE,"E8.49.5"),sQuery(id+"F0.wireOp",EDGE,"E8.50.0"),sQuery(id+"F0.wireOp",EDGE,"E8.50.1"),sQuery(id+"F0.wireOp",EDGE,"E8.50.2"),sQuery(id+"F0.wireOp",EDGE,"E8.50.3"),sQuery(id+"F0.wireOp",EDGE,"E8.50.4"),sQuery(id+"F0.wireOp",EDGE,"E8.50.5"),sQuery(id+"F0.wireOp",EDGE,"E8.51.0"),sQuery(id+"F0.wireOp",EDGE,"E8.51.1"),sQuery(id+"F0.wireOp",EDGE,"E8.51.2"),sQuery(id+"F0.wireOp",EDGE,"E8.51.3"),sQuery(id+"F0.wireOp",EDGE,"E8.51.4"),sQuery(id+"F0.wireOp",EDGE,"E8.51.5"),sQuery(id+"F0.wireOp",EDGE,"E8.52.0"),sQuery(id+"F0.wireOp",EDGE,"E8.52.1"),sQuery(id+"F0.wireOp",EDGE,"E8.52.2"),sQuery(id+"F0.wireOp",EDGE,"E8.52.3"),sQuery(id+"F0.wireOp",EDGE,"E8.52.4"),sQuery(id+"F0.wireOp",EDGE,"E8.52.5"),sQuery(id+"F0.wireOp",EDGE,"E8.53.0"),sQuery(id+"F0.wireOp",EDGE,"E8.53.1"),sQuery(id+"F0.wireOp",EDGE,"E8.53.2"),sQuery(id+"F0.wireOp",EDGE,"E8.53.3"),sQuery(id+"F0.wireOp",EDGE,"E8.53.4"),sQuery(id+"F0.wireOp",EDGE,"E8.53.5"),sQuery(id+"F0.wireOp",EDGE,"E8.54.0"),sQuery(id+"F0.wireOp",EDGE,"E8.54.1"),sQuery(id+"F0.wireOp",EDGE,"E8.54.2"),sQuery(id+"F0.wireOp",EDGE,"E8.54.3"),sQuery(id+"F0.wireOp",EDGE,"E8.54.4"),sQuery(id+"F0.wireOp",EDGE,"E8.54.5"),sQuery(id+"F0.wireOp",EDGE,"E8.55.0"),sQuery(id+"F0.wireOp",EDGE,"E8.55.1"),sQuery(id+"F0.wireOp",EDGE,"E8.55.2"),sQuery(id+"F0.wireOp",EDGE,"E8.55.3"),sQuery(id+"F0.wireOp",EDGE,"E8.55.4"),sQuery(id+"F0.wireOp",EDGE,"E8.55.5"),sQuery(id+"F0.wireOp",EDGE,"E8.56.0"),sQuery(id+"F0.wireOp",EDGE,"E8.56.1"),sQuery(id+"F0.wireOp",EDGE,"E8.56.2"),sQuery(id+"F0.wireOp",EDGE,"E8.56.3"),sQuery(id+"F0.wireOp",EDGE,"E8.56.4"),sQuery(id+"F0.wireOp",EDGE,"E8.56.5"),sQuery(id+"F0.wireOp",EDGE,"E8.57.0"),sQuery(id+"F0.wireOp",EDGE,"E8.57.1"),sQuery(id+"F0.wireOp",EDGE,"E8.57.2"),sQuery(id+"F0.wireOp",EDGE,"E8.57.3"),sQuery(id+"F0.wireOp",EDGE,"E8.57.4"),sQuery(id+"F0.wireOp",EDGE,"E8.57.5"),sQuery(id+"F0.wireOp",EDGE,"E8.58.0"),sQuery(id+"F0.wireOp",EDGE,"E8.58.1"),sQuery(id+"F0.wireOp",EDGE,"E8.58.2"),sQuery(id+"F0.wireOp",EDGE,"E8.58.3"),sQuery(id+"F0.wireOp",EDGE,"E8.58.4"),sQuery(id+"F0.wireOp",EDGE,"E8.58.5"),sQuery(id+"F0.wireOp",EDGE,"E8.59.0"),sQuery(id+"F0.wireOp",EDGE,"E8.59.1"),sQuery(id+"F0.wireOp",EDGE,"E8.59.2"),sQuery(id+"F0.wireOp",EDGE,"E8.59.3"),sQuery(id+"F0.wireOp",EDGE,"E8.59.4"),sQuery(id+"F0.wireOp",EDGE,"E8.59.5"),sQuery(id+"F0.wireOp",EDGE,"E8.60.0"),sQuery(id+"F0.wireOp",EDGE,"E8.60.1"),sQuery(id+"F0.wireOp",EDGE,"E8.60.2"),sQuery(id+"F0.wireOp",EDGE,"E8.60.3"),sQuery(id+"F0.wireOp",EDGE,"E8.60.4"),sQuery(id+"F0.wireOp",EDGE,"E8.60.5"),sQuery(id+"F0.wireOp",EDGE,"E8.61.0"),sQuery(id+"F0.wireOp",EDGE,"E8.61.1"),sQuery(id+"F0.wireOp",EDGE,"E8.61.2"),sQuery(id+"F0.wireOp",EDGE,"E8.61.3"),sQuery(id+"F0.wireOp",EDGE,"E8.61.4"),sQuery(id+"F0.wireOp",EDGE,"E8.61.5"),sQuery(id+"F0.wireOp",EDGE,"E8.62.0"),sQuery(id+"F0.wireOp",EDGE,"E8.62.1"),sQuery(id+"F0.wireOp",EDGE,"E8.62.2"),sQuery(id+"F0.wireOp",EDGE,"E8.62.3"),sQuery(id+"F0.wireOp",EDGE,"E8.62.4"),sQuery(id+"F0.wireOp",EDGE,"E8.62.5"),sQuery(id+"F0.wireOp",EDGE,"E8.63.0"),sQuery(id+"F0.wireOp",EDGE,"E8.63.1"),sQuery(id+"F0.wireOp",EDGE,"E8.63.2"),sQuery(id+"F0.wireOp",EDGE,"E8.63.3"),sQuery(id+"F0.wireOp",EDGE,"E8.63.4"),sQuery(id+"F0.wireOp",EDGE,"E8.63.5"),sQuery(id+"F0.wireOp",EDGE,"E8.64.0"),sQuery(id+"F0.wireOp",EDGE,"E8.64.1"),sQuery(id+"F0.wireOp",EDGE,"E8.64.2"),sQuery(id+"F0.wireOp",EDGE,"E8.64.3"),sQuery(id+"F0.wireOp",EDGE,"E8.64.4"),sQuery(id+"F0.wireOp",EDGE,"E8.64.5"),sQuery(id+"F0.wireOp",EDGE,"E8.65.0"),sQuery(id+"F0.wireOp",EDGE,"E8.65.1"),sQuery(id+"F0.wireOp",EDGE,"E8.65.2"),sQuery(id+"F0.wireOp",EDGE,"E8.65.3"),sQuery(id+"F0.wireOp",EDGE,"E8.65.4"),sQuery(id+"F0.wireOp",EDGE,"E8.65.5"),sQuery(id+"F0.wireOp",EDGE,"E8.66.0"),sQuery(id+"F0.wireOp",EDGE,"E8.66.1"),sQuery(id+"F0.wireOp",EDGE,"E8.66.2"),sQuery(id+"F0.wireOp",EDGE,"E8.66.3"),sQuery(id+"F0.wireOp",EDGE,"E8.66.4"),sQuery(id+"F0.wireOp",EDGE,"E8.66.5"),sQuery(id+"F0.wireOp",EDGE,"E8.67.0"),sQuery(id+"F0.wireOp",EDGE,"E8.67.1"),sQuery(id+"F0.wireOp",EDGE,"E8.67.2"),sQuery(id+"F0.wireOp",EDGE,"E8.67.3"),sQuery(id+"F0.wireOp",EDGE,"E8.67.4"),sQuery(id+"F0.wireOp",EDGE,"E8.67.5"),sQuery(id+"F0.wireOp",EDGE,"E8.68.0"),sQuery(id+"F0.wireOp",EDGE,"E8.68.1"),sQuery(id+"F0.wireOp",EDGE,"E8.68.2"),sQuery(id+"F0.wireOp",EDGE,"E8.68.3"),sQuery(id+"F0.wireOp",EDGE,"E8.68.4"),sQuery(id+"F0.wireOp",EDGE,"E8.68.5"),sQuery(id+"F0.wireOp",EDGE,"E8.69.0"),sQuery(id+"F0.wireOp",EDGE,"E8.69.1"),sQuery(id+"F0.wireOp",EDGE,"E8.69.2"),sQuery(id+"F0.wireOp",EDGE,"E8.69.3"),sQuery(id+"F0.wireOp",EDGE,"E8.69.4"),sQuery(id+"F0.wireOp",EDGE,"E8.69.5"),sQuery(id+"F0.wireOp",EDGE,"E8.70.0"),sQuery(id+"F0.wireOp",EDGE,"E8.70.1"),sQuery(id+"F0.wireOp",EDGE,"E8.70.2"),sQuery(id+"F0.wireOp",EDGE,"E8.70.3"),sQuery(id+"F0.wireOp",EDGE,"E8.70.4"),sQuery(id+"F0.wireOp",EDGE,"E8.70.5"),sQuery(id+"F0.wireOp",EDGE,"E8.71.0"),sQuery(id+"F0.wireOp",EDGE,"E8.71.1"),sQuery(id+"F0.wireOp",EDGE,"E8.71.2"),sQuery(id+"F0.wireOp",EDGE,"E8.71.3"),sQuery(id+"F0.wireOp",EDGE,"E8.71.4"),sQuery(id+"F0.wireOp",EDGE,"E8.71.5"),sQuery(id+"F0.wireOp",EDGE,"E9")])]});
            hole(context, id + "F5", {"style" : HoleStyle.SIMPLE, "endStyle" : HoleEndStyle.THROUGH, "holeDiameter" : 0.25 * mm, "locations" : qUnion([Q0, Q1, Q2]), "scope" : qUnion([Q3]), "isTappedThrough" : true});
        }
    });
